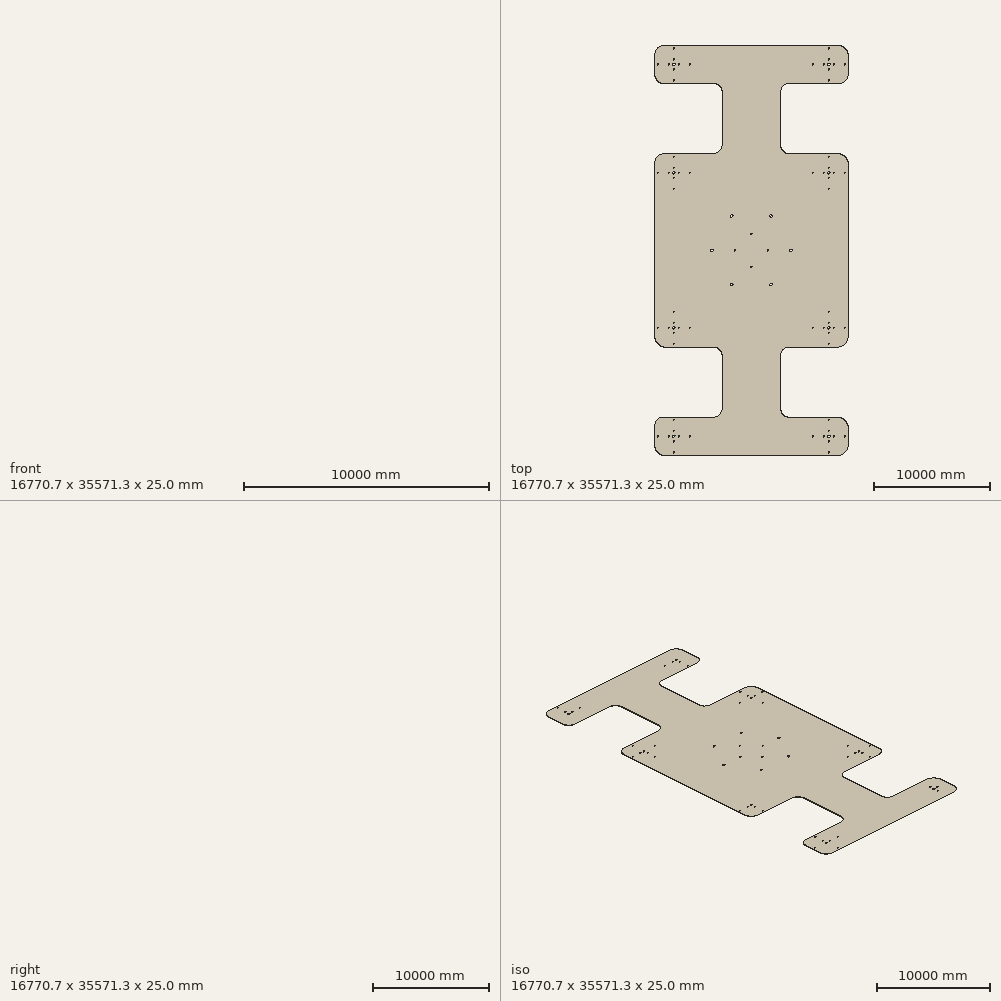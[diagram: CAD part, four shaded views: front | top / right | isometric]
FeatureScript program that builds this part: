
annotation { "Feature Type Name" : "Feature", "Feature Type Description" : "" }
export const myFeature = defineFeature(function(context is Context, id is Id, definition is map)
    precondition{}
    {
        {
            var Q0;
            Q0=qCreatedBy(makeId("Top.planeOp"),FACE);
            var sketch = newSketch(context, id + "F0", { "sketchPlane" : qUnion([Q0])});
            skLineSegment(sketch, "E0", {"start": v(-53625.62, -35381.23) * mm, "end": v(18764.38, -35381.23) * mm});
            skLineSegment(sketch, "E1", {"start": v(-52609.62, -34873.23) * mm, "end": v(17748.38, -34873.23) * mm});
            skLineSegment(sketch, "E2", {"start": v(-52609.62, -34767.82) * mm, "end": v(17748.38, -34767.82) * mm});
            skLineSegment(sketch, "E3", {"start": v(-52609.62, -34978.64) * mm, "end": v(17748.38, -34978.64) * mm});
            skLineSegment(sketch, "E4", {"start": v(-52609.62, -34365.23) * mm, "end": v(17748.38, -34365.23) * mm});
            skLineSegment(sketch, "E5", {"start": v(18764.38, -35381.23) * mm, "end": v(18764.38, -28777.23) * mm});
            skLineSegment(sketch, "E6", {"start": v(18256.38, -35381.23) * mm, "end": v(18256.38, -28777.23) * mm});
            skLineSegment(sketch, "E7", {"start": v(18150.97, -35381.23) * mm, "end": v(18150.97, -28777.23) * mm});
            skLineSegment(sketch, "E8", {"start": v(18361.79, -35381.23) * mm, "end": v(18361.79, -28777.23) * mm});
            skLineSegment(sketch, "E9", {"start": v(17748.38, -35381.23) * mm, "end": v(17748.38, -28777.23) * mm});
            skLineSegment(sketch, "E10", {"start": v(-53625.62, -35381.23) * mm, "end": v(-53625.62, -28777.23) * mm});
            skLineSegment(sketch, "E11", {"start": v(-53117.62, -35381.23) * mm, "end": v(-53117.62, -28777.23) * mm});
            skLineSegment(sketch, "E12", {"start": v(-53012.21, -35381.23) * mm, "end": v(-53012.21, -28777.23) * mm});
            skLineSegment(sketch, "E13", {"start": v(-53223.03, -35381.23) * mm, "end": v(-53223.03, -28777.23) * mm});
            skLineSegment(sketch, "E14", {"start": v(-52609.62, -35381.23) * mm, "end": v(-52609.62, -28777.23) * mm});
            skLineSegment(sketch, "E15", {"start": v(-52609.62, -29793.23) * mm, "end": v(17748.38, -29793.23) * mm});
            skLineSegment(sketch, "E16", {"start": v(-52609.62, -29285.23) * mm, "end": v(17748.38, -29285.23) * mm});
            skLineSegment(sketch, "E17", {"start": v(-52609.62, -29179.82) * mm, "end": v(17748.38, -29179.82) * mm});
            skLineSegment(sketch, "E18", {"start": v(-52609.62, -29390.64) * mm, "end": v(17748.38, -29390.64) * mm});
            skLineSegment(sketch, "E19", {"start": v(-53625.62, -28777.23) * mm, "end": v(18764.38, -28777.23) * mm});
            skLineSegment(sketch, "E20", {"start": v(15843.38, -6425.23) * mm, "end": v(15843.38, -17601.23) * mm});
            skLineSegment(sketch, "E21", {"start": v(15335.38, -6425.23) * mm, "end": v(15335.38, -17601.23) * mm});
            skLineSegment(sketch, "E22", {"start": v(14827.38, -6425.23) * mm, "end": v(14827.38, -17601.23) * mm});
            skLineSegment(sketch, "E23", {"start": v(15229.97, -6425.23) * mm, "end": v(15229.97, -17601.23) * mm});
            skLineSegment(sketch, "E24", {"start": v(15440.79, -6425.23) * mm, "end": v(15440.79, -17601.23) * mm});
            skLineSegment(sketch, "E25", {"start": v(-5492.62, -6425.23) * mm, "end": v(-5492.62, -17601.23) * mm});
            skLineSegment(sketch, "E26", {"start": v(-6000.62, -6425.23) * mm, "end": v(-6000.62, -17601.23) * mm});
            skLineSegment(sketch, "E27", {"start": v(-5895.21, -6425.23) * mm, "end": v(-5895.21, -17601.23) * mm});
            skLineSegment(sketch, "E28", {"start": v(-6106.03, -6425.23) * mm, "end": v(-6106.03, -17601.23) * mm});
            skLineSegment(sketch, "E29", {"start": v(-6508.62, -6425.23) * mm, "end": v(-6508.62, -17601.23) * mm});
            skLineSegment(sketch, "E30", {"start": v(15843.38, -28777.23) * mm, "end": v(15843.38, -17601.23) * mm});
            skLineSegment(sketch, "E31", {"start": v(15335.38, -28777.23) * mm, "end": v(15335.38, -17601.23) * mm});
            skLineSegment(sketch, "E32", {"start": v(15440.79, -28777.23) * mm, "end": v(15440.79, -17601.23) * mm});
            skLineSegment(sketch, "E33", {"start": v(15229.97, -28777.23) * mm, "end": v(15229.97, -17601.23) * mm});
            skLineSegment(sketch, "E34", {"start": v(14827.38, -28777.23) * mm, "end": v(14827.38, -17601.23) * mm});
            skLineSegment(sketch, "E35", {"start": v(-5492.62, -28777.23) * mm, "end": v(-5492.62, -17601.23) * mm});
            skLineSegment(sketch, "E36", {"start": v(-6000.62, -28777.23) * mm, "end": v(-6000.62, -17601.23) * mm});
            skLineSegment(sketch, "E37", {"start": v(-5895.21, -28777.23) * mm, "end": v(-5895.21, -17601.23) * mm});
            skLineSegment(sketch, "E38", {"start": v(-6106.03, -28777.23) * mm, "end": v(-6106.03, -17601.23) * mm});
            skLineSegment(sketch, "E39", {"start": v(-6508.62, -28777.23) * mm, "end": v(-6508.62, -17601.23) * mm});
            skLineSegment(sketch, "E40", {"start": v(-17430.62, -17601.23) * mm, "end": v(15843.38, -17601.23) * mm});
            skLineSegment(sketch, "E41", {"start": v(-10826.62, -29793.23) * mm, "end": v(15843.38, -29793.23) * mm});
            skLineSegment(sketch, "E42", {"start": v(-10826.62, -29285.23) * mm, "end": v(15843.38, -29285.23) * mm});
            skLineSegment(sketch, "E43", {"start": v(-10826.62, -29179.82) * mm, "end": v(15843.38, -29179.82) * mm});
            skLineSegment(sketch, "E44", {"start": v(-10826.62, -29390.64) * mm, "end": v(15843.38, -29390.64) * mm});
            skLineSegment(sketch, "E45", {"start": v(-10826.62, -28777.23) * mm, "end": v(15843.38, -28777.23) * mm});
            skLineSegment(sketch, "E46", {"start": v(-10826.62, -5409.23) * mm, "end": v(15843.38, -5409.23) * mm});
            skLineSegment(sketch, "E47", {"start": v(-10826.62, -5917.23) * mm, "end": v(15843.38, -5917.23) * mm});
            skLineSegment(sketch, "E48", {"start": v(-10826.62, -6022.64) * mm, "end": v(15843.38, -6022.64) * mm});
            skLineSegment(sketch, "E49", {"start": v(-10826.62, -5811.82) * mm, "end": v(15843.38, -5811.82) * mm});
            skLineSegment(sketch, "E50", {"start": v(-10826.62, -6425.23) * mm, "end": v(15843.38, -6425.23) * mm});
            skLineSegment(sketch, "E51", {"start": v(15843.38, -5409.23) * mm, "end": v(15843.38, -6425.23) * mm});
            skLineSegment(sketch, "E52", {"start": v(15843.38, -28777.23) * mm, "end": v(15843.38, -29793.23) * mm});
            skLineSegment(sketch, "E53", {"start": v(-10826.62, -5409.23) * mm, "end": v(-10826.62, -6425.23) * mm});
            skLineSegment(sketch, "E54", {"start": v(-10826.62, -28777.23) * mm, "end": v(-10826.62, -29793.23) * mm});
            skLineSegment(sketch, "E55", {"start": v(-50704.62, -6425.23) * mm, "end": v(-50704.62, -17601.23) * mm});
            skLineSegment(sketch, "E56", {"start": v(-50196.62, -6425.23) * mm, "end": v(-50196.62, -17601.23) * mm});
            skLineSegment(sketch, "E57", {"start": v(-49688.62, -6425.23) * mm, "end": v(-49688.62, -17601.23) * mm});
            skLineSegment(sketch, "E58", {"start": v(-50091.21, -6425.23) * mm, "end": v(-50091.21, -17601.23) * mm});
            skLineSegment(sketch, "E59", {"start": v(-50302.03, -6425.23) * mm, "end": v(-50302.03, -17601.23) * mm});
            skLineSegment(sketch, "E60", {"start": v(-29368.62, -6425.23) * mm, "end": v(-29368.62, -17601.23) * mm});
            skLineSegment(sketch, "E61", {"start": v(-28860.62, -6425.23) * mm, "end": v(-28860.62, -17601.23) * mm});
            skLineSegment(sketch, "E62", {"start": v(-28966.03, -6425.23) * mm, "end": v(-28966.03, -17601.23) * mm});
            skLineSegment(sketch, "E63", {"start": v(-28755.21, -6425.23) * mm, "end": v(-28755.21, -17601.23) * mm});
            skLineSegment(sketch, "E64", {"start": v(-28352.62, -6425.23) * mm, "end": v(-28352.62, -17601.23) * mm});
            skLineSegment(sketch, "E65", {"start": v(-50704.62, -28777.23) * mm, "end": v(-50704.62, -17601.23) * mm});
            skLineSegment(sketch, "E66", {"start": v(-50196.62, -28777.23) * mm, "end": v(-50196.62, -17601.23) * mm});
            skLineSegment(sketch, "E67", {"start": v(-50302.03, -28777.23) * mm, "end": v(-50302.03, -17601.23) * mm});
            skLineSegment(sketch, "E68", {"start": v(-50091.21, -28777.23) * mm, "end": v(-50091.21, -17601.23) * mm});
            skLineSegment(sketch, "E69", {"start": v(-49688.62, -28777.23) * mm, "end": v(-49688.62, -17601.23) * mm});
            skLineSegment(sketch, "E70", {"start": v(-29368.62, -28777.23) * mm, "end": v(-29368.62, -17601.23) * mm});
            skLineSegment(sketch, "E71", {"start": v(-28860.62, -28777.23) * mm, "end": v(-28860.62, -17601.23) * mm});
            skLineSegment(sketch, "E72", {"start": v(-28966.03, -28777.23) * mm, "end": v(-28966.03, -17601.23) * mm});
            skLineSegment(sketch, "E73", {"start": v(-28755.21, -28777.23) * mm, "end": v(-28755.21, -17601.23) * mm});
            skLineSegment(sketch, "E74", {"start": v(-28352.62, -28777.23) * mm, "end": v(-28352.62, -17601.23) * mm});
            skLineSegment(sketch, "E75", {"start": v(-17430.62, -17601.23) * mm, "end": v(-50704.62, -17601.23) * mm});
            skLineSegment(sketch, "E76", {"start": v(-24034.62, -29793.23) * mm, "end": v(-50704.62, -29793.23) * mm});
            skLineSegment(sketch, "E77", {"start": v(-24034.62, -29285.23) * mm, "end": v(-50704.62, -29285.23) * mm});
            skLineSegment(sketch, "E78", {"start": v(-24034.62, -29179.82) * mm, "end": v(-50704.62, -29179.82) * mm});
            skLineSegment(sketch, "E79", {"start": v(-24034.62, -29390.64) * mm, "end": v(-50704.62, -29390.64) * mm});
            skLineSegment(sketch, "E80", {"start": v(-24034.62, -28777.23) * mm, "end": v(-50704.62, -28777.23) * mm});
            skLineSegment(sketch, "E81", {"start": v(-24034.62, -5409.23) * mm, "end": v(-50704.62, -5409.23) * mm});
            skLineSegment(sketch, "E82", {"start": v(-24034.62, -5917.23) * mm, "end": v(-50704.62, -5917.23) * mm});
            skLineSegment(sketch, "E83", {"start": v(-24034.62, -6022.64) * mm, "end": v(-50704.62, -6022.64) * mm});
            skLineSegment(sketch, "E84", {"start": v(-24034.62, -5811.82) * mm, "end": v(-50704.62, -5811.82) * mm});
            skLineSegment(sketch, "E85", {"start": v(-24034.62, -6425.23) * mm, "end": v(-50704.62, -6425.23) * mm});
            skLineSegment(sketch, "E86", {"start": v(-50704.62, -5409.23) * mm, "end": v(-50704.62, -6425.23) * mm});
            skLineSegment(sketch, "E87", {"start": v(-50704.62, -28777.23) * mm, "end": v(-50704.62, -29793.23) * mm});
            skLineSegment(sketch, "E88", {"start": v(-24034.62, -5409.23) * mm, "end": v(-24034.62, -6425.23) * mm});
            skLineSegment(sketch, "E89", {"start": v(-24034.62, -28777.23) * mm, "end": v(-24034.62, -29793.23) * mm});
            skLineSegment(sketch, "E90", {"start": v(-17430.62, 7443.17) * mm, "end": v(-17430.62, -41629.63) * mm});
            skLineSegment(sketch, "E91", {"start": v(-14382.62, -7441.23) * mm, "end": v(-14382.62, -8457.23) * mm});
            skLineSegment(sketch, "E92", {"start": v(-28352.62, -27761.23) * mm, "end": v(-6508.62, -27761.23) * mm});
            skLineSegment(sketch, "E93", {"start": v(-28352.62, -28269.23) * mm, "end": v(-6508.62, -28269.23) * mm});
            skLineSegment(sketch, "E94", {"start": v(-28352.62, -28163.82) * mm, "end": v(-6508.62, -28163.82) * mm});
            skLineSegment(sketch, "E95", {"start": v(-28352.62, -28374.64) * mm, "end": v(-6508.62, -28374.64) * mm});
            skLineSegment(sketch, "E96", {"start": v(-28352.62, -28777.23) * mm, "end": v(-6508.62, -28777.23) * mm});
            skLineSegment(sketch, "E97", {"start": v(-5492.62, -27761.23) * mm, "end": v(14827.38, -27761.23) * mm});
            skLineSegment(sketch, "E98", {"start": v(-10191.62, -28269.23) * mm, "end": v(14827.38, -28269.23) * mm});
            skLineSegment(sketch, "E99", {"start": v(-5492.62, -28163.82) * mm, "end": v(14827.38, -28163.82) * mm});
            skLineSegment(sketch, "E100", {"start": v(-5492.62, -28374.64) * mm, "end": v(14827.38, -28374.64) * mm});
            skLineSegment(sketch, "E101", {"start": v(-10191.62, -28777.23) * mm, "end": v(14827.38, -28777.23) * mm});
            skLineSegment(sketch, "E102", {"start": v(-49688.62, -27761.23) * mm, "end": v(-29368.62, -27761.23) * mm});
            skLineSegment(sketch, "E103", {"start": v(-49688.62, -28269.23) * mm, "end": v(-29368.62, -28269.23) * mm});
            skLineSegment(sketch, "E104", {"start": v(-49688.62, -28163.82) * mm, "end": v(-29368.62, -28163.82) * mm});
            skLineSegment(sketch, "E105", {"start": v(-49688.62, -28374.64) * mm, "end": v(-29368.62, -28374.64) * mm});
            skLineSegment(sketch, "E106", {"start": v(-49688.62, -28777.23) * mm, "end": v(-29368.62, -28777.23) * mm});
            skLineSegment(sketch, "E107", {"start": v(-28352.62, -7441.23) * mm, "end": v(-6508.62, -7441.23) * mm});
            skLineSegment(sketch, "E108", {"start": v(-28352.62, -6933.23) * mm, "end": v(-6508.62, -6933.23) * mm});
            skLineSegment(sketch, "E109", {"start": v(-28352.62, -7038.64) * mm, "end": v(-6508.62, -7038.64) * mm});
            skLineSegment(sketch, "E110", {"start": v(-28352.62, -6827.82) * mm, "end": v(-6508.62, -6827.82) * mm});
            skLineSegment(sketch, "E111", {"start": v(-28352.62, -6425.23) * mm, "end": v(-6508.62, -6425.23) * mm});
            skLineSegment(sketch, "E112", {"start": v(-5492.62, -7441.23) * mm, "end": v(14827.38, -7441.23) * mm});
            skLineSegment(sketch, "E113", {"start": v(-10191.62, -6933.23) * mm, "end": v(14827.38, -6933.23) * mm});
            skLineSegment(sketch, "E114", {"start": v(-5492.62, -7038.64) * mm, "end": v(14827.38, -7038.64) * mm});
            skLineSegment(sketch, "E115", {"start": v(-5492.62, -6827.82) * mm, "end": v(14827.38, -6827.82) * mm});
            skLineSegment(sketch, "E116", {"start": v(-49688.62, -7441.23) * mm, "end": v(-29368.62, -7441.23) * mm});
            skLineSegment(sketch, "E117", {"start": v(-49688.62, -6933.23) * mm, "end": v(-29368.62, -6933.23) * mm});
            skLineSegment(sketch, "E118", {"start": v(-49688.62, -7038.64) * mm, "end": v(-29368.62, -7038.64) * mm});
            skLineSegment(sketch, "E119", {"start": v(-49688.62, -6827.82) * mm, "end": v(-29368.62, -6827.82) * mm});
            skLineSegment(sketch, "E120", {"start": v(-14382.62, -8457.23) * mm, "end": v(-6508.62, -8457.23) * mm});
            skLineSegment(sketch, "E121", {"start": v(-14382.62, -7949.23) * mm, "end": v(-6508.62, -7949.23) * mm});
            skLineSegment(sketch, "E122", {"start": v(-14382.62, -8054.64) * mm, "end": v(-6508.62, -8054.64) * mm});
            skLineSegment(sketch, "E123", {"start": v(-14382.62, -7843.82) * mm, "end": v(-6508.62, -7843.82) * mm});
            skCircle(sketch, "E124", {"center": v(51353.06, -10870.23) * mm, "radius": 1397 * mm});
            skLineSegment(sketch, "E125", {"start": v(51353.06, -9219.23) * mm, "end": v(51353.06, -12521.23) * mm});
            skLineSegment(sketch, "E126", {"start": v(49716.24, -10870.23) * mm, "end": v(53018.24, -10870.23) * mm});
            skLineSegment(sketch, "E127", {"start": v(52369.06, -10870.23) * mm, "end": v(50337.06, -10870.23) * mm});
            skLineSegment(sketch, "E128", {"start": v(51353.06, -9854.23) * mm, "end": v(51353.06, -11886.23) * mm});
            skCircle(sketch, "E129", {"center": v(51353.06, -10870.23) * mm, "radius": 444.5 * mm});
            skCircle(sketch, "E130", {"center": v(51371.33, -10392.3) * mm, "radius": 6.35 * mm});
            skLineSegment(sketch, "E131", {"start": v(51353.06, -10324.13) * mm, "end": v(51353.06, -10527.33) * mm});
            skLineSegment(sketch, "E132", {"start": v(51251.46, -10425.73) * mm, "end": v(51454.66, -10425.73) * mm});
            skCircle(sketch, "E133", {"center": v(51353.06, -10425.73) * mm, "radius": 62.45 * mm});
            skArc(sketch, "E134", {"start": v(51276.86, -10425.73) * mm, "mid": v(51299.18, -10479.61) * mm, "end": v(51353.06, -10501.93) * mm});
            skCircle(sketch, "E135", {"center": v(50875.13, -10851.96) * mm, "radius": 6.35 * mm});
            skLineSegment(sketch, "E136", {"start": v(50806.96, -10870.23) * mm, "end": v(51010.16, -10870.23) * mm});
            skLineSegment(sketch, "E137", {"start": v(50908.56, -10971.83) * mm, "end": v(50908.56, -10768.63) * mm});
            skCircle(sketch, "E138", {"center": v(50908.56, -10870.23) * mm, "radius": 62.45 * mm});
            skArc(sketch, "E139", {"start": v(50908.56, -10946.43) * mm, "mid": v(50962.45, -10924.11) * mm, "end": v(50984.76, -10870.23) * mm});
            skCircle(sketch, "E140", {"center": v(51334.8, -11348.17) * mm, "radius": 6.35 * mm});
            skLineSegment(sketch, "E141", {"start": v(51353.06, -11416.33) * mm, "end": v(51353.06, -11213.13) * mm});
            skLineSegment(sketch, "E142", {"start": v(51454.66, -11314.73) * mm, "end": v(51251.46, -11314.73) * mm});
            skCircle(sketch, "E143", {"center": v(51353.06, -11314.73) * mm, "radius": 62.45 * mm});
            skArc(sketch, "E144", {"start": v(51429.26, -11314.73) * mm, "mid": v(51406.95, -11260.85) * mm, "end": v(51353.06, -11238.53) * mm});
            skCircle(sketch, "E145", {"center": v(51831, -10888.5) * mm, "radius": 6.35 * mm});
            skLineSegment(sketch, "E146", {"start": v(51899.16, -10870.23) * mm, "end": v(51695.96, -10870.23) * mm});
            skLineSegment(sketch, "E147", {"start": v(51797.56, -10768.63) * mm, "end": v(51797.56, -10971.83) * mm});
            skCircle(sketch, "E148", {"center": v(51797.56, -10870.23) * mm, "radius": 62.45 * mm});
            skArc(sketch, "E149", {"start": v(51797.56, -10794.03) * mm, "mid": v(51743.68, -10816.35) * mm, "end": v(51721.36, -10870.23) * mm});
            skCircle(sketch, "E150", {"center": v(51380.17, -10885.04) * mm, "radius": 6.35 * mm});
            skCircle(sketch, "E151", {"center": v(51353.06, -10870.23) * mm, "radius": 108.79 * mm});
            skArc(sketch, "E152", {"start": v(51340.22, -10747.43) * mm, "mid": v(51257.14, -10792.48) * mm, "end": v(51230.26, -10883.08) * mm});
            skLineSegment(sketch, "E153", {"start": v(51502, -10870.23) * mm, "end": v(51204.12, -10870.23) * mm});
            skLineSegment(sketch, "E154", {"start": v(51353.06, -10721.28) * mm, "end": v(51353.06, -11019.18) * mm});
            skLineSegment(sketch, "E155", {"start": v(52496.06, -10870.23) * mm, "end": v(50210.06, -10870.23) * mm});
            skLineSegment(sketch, "E156", {"start": v(51353.06, -12394.23) * mm, "end": v(51353.06, -12140.23) * mm});
            skLineSegment(sketch, "E157", {"start": v(51480.06, -12267.23) * mm, "end": v(51226.06, -12267.23) * mm});
            skCircle(sketch, "E158", {"center": v(51353.06, -12267.23) * mm, "radius": 62.45 * mm});
            skArc(sketch, "E159", {"start": v(51429.26, -12267.23) * mm, "mid": v(51406.95, -12213.35) * mm, "end": v(51353.06, -12191.03) * mm});
            skLineSegment(sketch, "E160", {"start": v(49956.06, -10997.23) * mm, "end": v(49956.06, -10743.23) * mm});
            skLineSegment(sketch, "E161", {"start": v(50083.06, -10870.23) * mm, "end": v(49829.06, -10870.23) * mm});
            skCircle(sketch, "E162", {"center": v(49956.06, -10870.23) * mm, "radius": 62.45 * mm});
            skArc(sketch, "E163", {"start": v(50032.26, -10870.23) * mm, "mid": v(50009.95, -10816.35) * mm, "end": v(49956.06, -10794.03) * mm});
            skLineSegment(sketch, "E164", {"start": v(51353.06, -9600.23) * mm, "end": v(51353.06, -9346.23) * mm});
            skLineSegment(sketch, "E165", {"start": v(51480.06, -9473.23) * mm, "end": v(51226.06, -9473.23) * mm});
            skCircle(sketch, "E166", {"center": v(51353.06, -9473.23) * mm, "radius": 62.45 * mm});
            skArc(sketch, "E167", {"start": v(51429.26, -9473.23) * mm, "mid": v(51406.95, -9419.35) * mm, "end": v(51353.06, -9397.03) * mm});
            skLineSegment(sketch, "E168", {"start": v(52750.06, -10997.23) * mm, "end": v(52750.06, -10743.23) * mm});
            skLineSegment(sketch, "E169", {"start": v(52877.06, -10870.23) * mm, "end": v(52623.06, -10870.23) * mm});
            skCircle(sketch, "E170", {"center": v(52750.06, -10870.23) * mm, "radius": 62.45 * mm});
            skArc(sketch, "E171", {"start": v(52826.26, -10870.23) * mm, "mid": v(52803.95, -10816.35) * mm, "end": v(52750.06, -10794.03) * mm});
            skLineSegment(sketch, "E172", {"start": v(44622.06, -26607.16) * mm, "end": v(44622.06, 178.77) * mm});
            skLineSegment(sketch, "E173", {"start": v(35628.8, -17601.23) * mm, "end": v(53625.62, -17601.23) * mm});
            skCircle(sketch, "E174", {"center": v(44622.06, -17601.23) * mm, "radius": 3429 * mm});
            skCircle(sketch, "E175", {"center": v(44622.06, -17601.23) * mm, "radius": 1397 * mm});
            skLineSegment(sketch, "E176", {"start": v(42971.06, -17601.23) * mm, "end": v(46273.06, -17601.23) * mm});
            skLineSegment(sketch, "E177", {"start": v(44622.06, -15950.23) * mm, "end": v(44622.06, -19252.23) * mm});
            skLineSegment(sketch, "E178", {"start": v(44622.06, -18617.23) * mm, "end": v(44622.06, -16585.23) * mm});
            skLineSegment(sketch, "E179", {"start": v(43606.06, -17601.23) * mm, "end": v(45638.06, -17601.23) * mm});
            skLineSegment(sketch, "E180", {"start": v(44622.06, -18744.23) * mm, "end": v(44622.06, -16458.23) * mm});
            skLineSegment(sketch, "E181", {"start": v(43098.06, -17601.23) * mm, "end": v(43352.06, -17601.23) * mm});
            skLineSegment(sketch, "E182", {"start": v(43225.06, -17474.23) * mm, "end": v(43225.06, -17728.23) * mm});
            skCircle(sketch, "E183", {"center": v(43225.06, -17601.23) * mm, "radius": 62.45 * mm});
            skArc(sketch, "E184", {"start": v(43301.26, -17601.23) * mm, "mid": v(43278.95, -17547.35) * mm, "end": v(43225.06, -17525.03) * mm});
            skLineSegment(sketch, "E185", {"start": v(44495.06, -18998.23) * mm, "end": v(44749.06, -18998.23) * mm});
            skLineSegment(sketch, "E186", {"start": v(44622.06, -18871.23) * mm, "end": v(44622.06, -19125.23) * mm});
            skCircle(sketch, "E187", {"center": v(44622.06, -18998.23) * mm, "radius": 62.45 * mm});
            skArc(sketch, "E188", {"start": v(44698.26, -18998.23) * mm, "mid": v(44675.95, -18944.35) * mm, "end": v(44622.06, -18922.03) * mm});
            skLineSegment(sketch, "E189", {"start": v(45892.06, -17601.23) * mm, "end": v(46146.06, -17601.23) * mm});
            skLineSegment(sketch, "E190", {"start": v(46019.06, -17474.23) * mm, "end": v(46019.06, -17728.23) * mm});
            skCircle(sketch, "E191", {"center": v(46019.06, -17601.23) * mm, "radius": 62.45 * mm});
            skArc(sketch, "E192", {"start": v(46095.26, -17601.23) * mm, "mid": v(46072.95, -17547.35) * mm, "end": v(46019.06, -17525.03) * mm});
            skLineSegment(sketch, "E193", {"start": v(44495.06, -16204.23) * mm, "end": v(44749.06, -16204.23) * mm});
            skLineSegment(sketch, "E194", {"start": v(44622.06, -16077.23) * mm, "end": v(44622.06, -16331.23) * mm});
            skCircle(sketch, "E195", {"center": v(44622.06, -16204.23) * mm, "radius": 62.45 * mm});
            skArc(sketch, "E196", {"start": v(44698.26, -16204.23) * mm, "mid": v(44675.95, -16150.35) * mm, "end": v(44622.06, -16128.03) * mm});
            skCircle(sketch, "E197", {"center": v(48051.06, -17601.23) * mm, "radius": 114.3 * mm});
            skCircle(sketch, "E198", {"center": v(48051.06, -17601.23) * mm, "radius": 177.8 * mm});
            skLineSegment(sketch, "E199", {"start": v(48051.06, -17839.99) * mm, "end": v(48051.06, -17362.47) * mm});
            skLineSegment(sketch, "E200", {"start": v(47812.3, -17601.23) * mm, "end": v(48289.82, -17601.23) * mm});
            skCircle(sketch, "E201", {"center": v(46336.56, -20570.83) * mm, "radius": 114.3 * mm});
            skCircle(sketch, "E202", {"center": v(46336.56, -20570.83) * mm, "radius": 177.8 * mm});
            skLineSegment(sketch, "E203", {"start": v(46129.8, -20690.21) * mm, "end": v(46543.34, -20451.45) * mm});
            skLineSegment(sketch, "E204", {"start": v(46217.18, -20364.06) * mm, "end": v(46455.94, -20777.6) * mm});
            skCircle(sketch, "E205", {"center": v(42907.56, -20570.83) * mm, "radius": 114.3 * mm});
            skCircle(sketch, "E206", {"center": v(42907.56, -20570.83) * mm, "radius": 177.8 * mm});
            skLineSegment(sketch, "E207", {"start": v(42700.8, -20451.45) * mm, "end": v(43114.34, -20690.21) * mm});
            skLineSegment(sketch, "E208", {"start": v(43026.94, -20364.06) * mm, "end": v(42788.18, -20777.6) * mm});
            skCircle(sketch, "E209", {"center": v(41193.06, -17601.23) * mm, "radius": 114.3 * mm});
            skCircle(sketch, "E210", {"center": v(41193.06, -17601.23) * mm, "radius": 177.8 * mm});
            skLineSegment(sketch, "E211", {"start": v(41193.06, -17362.47) * mm, "end": v(41193.06, -17839.99) * mm});
            skLineSegment(sketch, "E212", {"start": v(41431.82, -17601.23) * mm, "end": v(40954.3, -17601.23) * mm});
            skCircle(sketch, "E213", {"center": v(42907.56, -14631.63) * mm, "radius": 114.3 * mm});
            skCircle(sketch, "E214", {"center": v(42907.56, -14631.63) * mm, "radius": 177.8 * mm});
            skLineSegment(sketch, "E215", {"start": v(43114.34, -14512.25) * mm, "end": v(42700.8, -14751) * mm});
            skLineSegment(sketch, "E216", {"start": v(43026.94, -14838.4) * mm, "end": v(42788.18, -14424.86) * mm});
            skCircle(sketch, "E217", {"center": v(46336.56, -14631.63) * mm, "radius": 114.3 * mm});
            skCircle(sketch, "E218", {"center": v(46336.56, -14631.63) * mm, "radius": 177.8 * mm});
            skLineSegment(sketch, "E219", {"start": v(46543.34, -14751) * mm, "end": v(46129.8, -14512.25) * mm});
            skLineSegment(sketch, "E220", {"start": v(46217.18, -14838.4) * mm, "end": v(46455.94, -14424.86) * mm});
            skLineSegment(sketch, "E221", {"start": v(47162.06, -3885.23) * mm, "end": v(47162.06, -8457.23) * mm});
            skArc(sketch, "E222", {"start": v(47162.06, -8457.23) * mm, "mid": v(48462.88, -7918.41) * mm, "end": v(47924.06, -9219.23) * mm});
            skLineSegment(sketch, "E223", {"start": v(47924.06, -9219.23) * mm, "end": v(52242.06, -9219.23) * mm});
            skLineSegment(sketch, "E224", {"start": v(52242.06, -9219.23) * mm, "end": v(53004.06, -9981.23) * mm});
            skLineSegment(sketch, "E225", {"start": v(53004.06, -9981.23) * mm, "end": v(53004.06, -25221.23) * mm});
            skLineSegment(sketch, "E226", {"start": v(53004.06, -25221.23) * mm, "end": v(52242.06, -25983.23) * mm});
            skLineSegment(sketch, "E227", {"start": v(52242.06, -25983.23) * mm, "end": v(47924.06, -25983.23) * mm});
            skArc(sketch, "E228", {"start": v(47924.06, -25983.23) * mm, "mid": v(48462.88, -27284.05) * mm, "end": v(47162.06, -26745.23) * mm});
            skLineSegment(sketch, "E229", {"start": v(47162.06, -26745.23) * mm, "end": v(47162.06, -31317.23) * mm});
            skArc(sketch, "E230", {"start": v(47162.06, -31317.23) * mm, "mid": v(48462.88, -30778.41) * mm, "end": v(47924.06, -32079.23) * mm});
            skLineSegment(sketch, "E231", {"start": v(47924.06, -32079.23) * mm, "end": v(52242.06, -32079.23) * mm});
            skCircle(sketch, "E232", {"center": v(51353.06, -24332.23) * mm, "radius": 1397 * mm});
            skLineSegment(sketch, "E233", {"start": v(53004.06, -24332.23) * mm, "end": v(49702.06, -24332.23) * mm});
            skLineSegment(sketch, "E234", {"start": v(51353.06, -22695.4) * mm, "end": v(51353.06, -25997.4) * mm});
            skLineSegment(sketch, "E235", {"start": v(51353.06, -25348.23) * mm, "end": v(51353.06, -23316.23) * mm});
            skLineSegment(sketch, "E236", {"start": v(52369.06, -24332.23) * mm, "end": v(50337.06, -24332.23) * mm});
            skCircle(sketch, "E237", {"center": v(51353.06, -24332.23) * mm, "radius": 444.5 * mm});
            skCircle(sketch, "E238", {"center": v(51831, -24350.5) * mm, "radius": 6.35 * mm});
            skLineSegment(sketch, "E239", {"start": v(51899.16, -24332.23) * mm, "end": v(51695.96, -24332.23) * mm});
            skLineSegment(sketch, "E240", {"start": v(51797.56, -24230.63) * mm, "end": v(51797.56, -24433.83) * mm});
            skCircle(sketch, "E241", {"center": v(51797.56, -24332.23) * mm, "radius": 62.45 * mm});
            skArc(sketch, "E242", {"start": v(51797.56, -24256.03) * mm, "mid": v(51743.68, -24278.35) * mm, "end": v(51721.36, -24332.23) * mm});
            skCircle(sketch, "E243", {"center": v(51371.33, -23854.3) * mm, "radius": 6.35 * mm});
            skLineSegment(sketch, "E244", {"start": v(51353.06, -23786.13) * mm, "end": v(51353.06, -23989.33) * mm});
            skLineSegment(sketch, "E245", {"start": v(51251.46, -23887.73) * mm, "end": v(51454.66, -23887.73) * mm});
            skCircle(sketch, "E246", {"center": v(51353.06, -23887.73) * mm, "radius": 62.45 * mm});
            skArc(sketch, "E247", {"start": v(51276.86, -23887.73) * mm, "mid": v(51299.18, -23941.61) * mm, "end": v(51353.06, -23963.93) * mm});
            skCircle(sketch, "E248", {"center": v(50875.13, -24313.96) * mm, "radius": 6.35 * mm});
            skLineSegment(sketch, "E249", {"start": v(50806.96, -24332.23) * mm, "end": v(51010.16, -24332.23) * mm});
            skLineSegment(sketch, "E250", {"start": v(50908.56, -24433.83) * mm, "end": v(50908.56, -24230.63) * mm});
            skCircle(sketch, "E251", {"center": v(50908.56, -24332.23) * mm, "radius": 62.45 * mm});
            skArc(sketch, "E252", {"start": v(50908.56, -24408.43) * mm, "mid": v(50962.45, -24386.11) * mm, "end": v(50984.76, -24332.23) * mm});
            skCircle(sketch, "E253", {"center": v(51334.8, -24810.17) * mm, "radius": 6.35 * mm});
            skLineSegment(sketch, "E254", {"start": v(51353.06, -24878.33) * mm, "end": v(51353.06, -24675.13) * mm});
            skLineSegment(sketch, "E255", {"start": v(51454.66, -24776.73) * mm, "end": v(51251.46, -24776.73) * mm});
            skCircle(sketch, "E256", {"center": v(51353.06, -24776.73) * mm, "radius": 62.45 * mm});
            skArc(sketch, "E257", {"start": v(51429.26, -24776.73) * mm, "mid": v(51406.95, -24722.85) * mm, "end": v(51353.06, -24700.53) * mm});
            skCircle(sketch, "E258", {"center": v(51338.26, -24359.34) * mm, "radius": 6.35 * mm});
            skCircle(sketch, "E259", {"center": v(51353.06, -24332.23) * mm, "radius": 108.79 * mm});
            skArc(sketch, "E260", {"start": v(51475.87, -24319.38) * mm, "mid": v(51430.81, -24236.3) * mm, "end": v(51340.22, -24209.43) * mm});
            skLineSegment(sketch, "E261", {"start": v(51353.06, -24481.18) * mm, "end": v(51353.06, -24183.28) * mm});
            skLineSegment(sketch, "E262", {"start": v(51502, -24332.23) * mm, "end": v(51204.12, -24332.23) * mm});
            skLineSegment(sketch, "E263", {"start": v(51353.06, -25475.23) * mm, "end": v(51353.06, -23189.23) * mm});
            skLineSegment(sketch, "E264", {"start": v(49829.06, -24332.23) * mm, "end": v(50083.06, -24332.23) * mm});
            skLineSegment(sketch, "E265", {"start": v(49956.06, -24459.23) * mm, "end": v(49956.06, -24205.23) * mm});
            skCircle(sketch, "E266", {"center": v(49956.06, -24332.23) * mm, "radius": 62.45 * mm});
            skArc(sketch, "E267", {"start": v(49956.06, -24408.43) * mm, "mid": v(50009.95, -24386.11) * mm, "end": v(50032.26, -24332.23) * mm});
            skLineSegment(sketch, "E268", {"start": v(51226.06, -22935.23) * mm, "end": v(51480.06, -22935.23) * mm});
            skLineSegment(sketch, "E269", {"start": v(51353.06, -23062.23) * mm, "end": v(51353.06, -22808.23) * mm});
            skCircle(sketch, "E270", {"center": v(51353.06, -22935.23) * mm, "radius": 62.45 * mm});
            skArc(sketch, "E271", {"start": v(51353.06, -23011.43) * mm, "mid": v(51406.95, -22989.11) * mm, "end": v(51429.26, -22935.23) * mm});
            skLineSegment(sketch, "E272", {"start": v(52623.06, -24332.23) * mm, "end": v(52877.06, -24332.23) * mm});
            skLineSegment(sketch, "E273", {"start": v(52750.06, -24459.23) * mm, "end": v(52750.06, -24205.23) * mm});
            skCircle(sketch, "E274", {"center": v(52750.06, -24332.23) * mm, "radius": 62.45 * mm});
            skArc(sketch, "E275", {"start": v(52750.06, -24408.43) * mm, "mid": v(52803.95, -24386.11) * mm, "end": v(52826.26, -24332.23) * mm});
            skLineSegment(sketch, "E276", {"start": v(51226.06, -25729.23) * mm, "end": v(51480.06, -25729.23) * mm});
            skLineSegment(sketch, "E277", {"start": v(51353.06, -25856.23) * mm, "end": v(51353.06, -25602.23) * mm});
            skCircle(sketch, "E278", {"center": v(51353.06, -25729.23) * mm, "radius": 62.45 * mm});
            skArc(sketch, "E279", {"start": v(51353.06, -25805.43) * mm, "mid": v(51406.95, -25783.11) * mm, "end": v(51429.26, -25729.23) * mm});
            skCircle(sketch, "E280", {"center": v(37891.06, -24332.23) * mm, "radius": 1397 * mm});
            skLineSegment(sketch, "E281", {"start": v(37891.06, -25983.23) * mm, "end": v(37891.06, -22681.23) * mm});
            skLineSegment(sketch, "E282", {"start": v(39527.89, -24332.23) * mm, "end": v(36225.89, -24332.23) * mm});
            skLineSegment(sketch, "E283", {"start": v(36875.06, -24332.23) * mm, "end": v(38907.06, -24332.23) * mm});
            skLineSegment(sketch, "E284", {"start": v(37891.06, -25348.23) * mm, "end": v(37891.06, -23316.23) * mm});
            skCircle(sketch, "E285", {"center": v(37891.06, -24332.23) * mm, "radius": 444.5 * mm});
            skCircle(sketch, "E286", {"center": v(37872.8, -24810.17) * mm, "radius": 6.35 * mm});
            skLineSegment(sketch, "E287", {"start": v(37891.06, -24878.33) * mm, "end": v(37891.06, -24675.13) * mm});
            skLineSegment(sketch, "E288", {"start": v(37992.66, -24776.73) * mm, "end": v(37789.46, -24776.73) * mm});
            skCircle(sketch, "E289", {"center": v(37891.06, -24776.73) * mm, "radius": 62.45 * mm});
            skArc(sketch, "E290", {"start": v(37967.26, -24776.73) * mm, "mid": v(37944.95, -24722.85) * mm, "end": v(37891.06, -24700.53) * mm});
            skCircle(sketch, "E291", {"center": v(38369, -24350.5) * mm, "radius": 6.35 * mm});
            skLineSegment(sketch, "E292", {"start": v(38437.16, -24332.23) * mm, "end": v(38233.96, -24332.23) * mm});
            skLineSegment(sketch, "E293", {"start": v(38335.56, -24230.63) * mm, "end": v(38335.56, -24433.83) * mm});
            skCircle(sketch, "E294", {"center": v(38335.56, -24332.23) * mm, "radius": 62.45 * mm});
            skArc(sketch, "E295", {"start": v(38335.56, -24256.03) * mm, "mid": v(38281.68, -24278.35) * mm, "end": v(38259.36, -24332.23) * mm});
            skCircle(sketch, "E296", {"center": v(37909.33, -23854.3) * mm, "radius": 6.35 * mm});
            skLineSegment(sketch, "E297", {"start": v(37891.06, -23786.13) * mm, "end": v(37891.06, -23989.33) * mm});
            skLineSegment(sketch, "E298", {"start": v(37789.46, -23887.73) * mm, "end": v(37992.66, -23887.73) * mm});
            skCircle(sketch, "E299", {"center": v(37891.06, -23887.73) * mm, "radius": 62.45 * mm});
            skArc(sketch, "E300", {"start": v(37814.86, -23887.73) * mm, "mid": v(37837.18, -23941.61) * mm, "end": v(37891.06, -23963.93) * mm});
            skCircle(sketch, "E301", {"center": v(37413.13, -24313.96) * mm, "radius": 6.35 * mm});
            skLineSegment(sketch, "E302", {"start": v(37344.96, -24332.23) * mm, "end": v(37548.16, -24332.23) * mm});
            skLineSegment(sketch, "E303", {"start": v(37446.56, -24433.83) * mm, "end": v(37446.56, -24230.63) * mm});
            skCircle(sketch, "E304", {"center": v(37446.56, -24332.23) * mm, "radius": 62.45 * mm});
            skArc(sketch, "E305", {"start": v(37446.56, -24408.43) * mm, "mid": v(37500.45, -24386.11) * mm, "end": v(37522.76, -24332.23) * mm});
            skCircle(sketch, "E306", {"center": v(37863.96, -24317.42) * mm, "radius": 6.35 * mm});
            skCircle(sketch, "E307", {"center": v(37891.06, -24332.23) * mm, "radius": 108.79 * mm});
            skArc(sketch, "E308", {"start": v(37903.91, -24455.03) * mm, "mid": v(37986.99, -24409.98) * mm, "end": v(38013.87, -24319.38) * mm});
            skLineSegment(sketch, "E309", {"start": v(37742.12, -24332.23) * mm, "end": v(38040, -24332.23) * mm});
            skLineSegment(sketch, "E310", {"start": v(37891.06, -24481.18) * mm, "end": v(37891.06, -24183.28) * mm});
            skLineSegment(sketch, "E311", {"start": v(36748.06, -24332.23) * mm, "end": v(39034.06, -24332.23) * mm});
            skLineSegment(sketch, "E312", {"start": v(37891.06, -22808.23) * mm, "end": v(37891.06, -23062.23) * mm});
            skLineSegment(sketch, "E313", {"start": v(37764.06, -22935.23) * mm, "end": v(38018.06, -22935.23) * mm});
            skCircle(sketch, "E314", {"center": v(37891.06, -22935.23) * mm, "radius": 62.45 * mm});
            skArc(sketch, "E315", {"start": v(37814.86, -22935.23) * mm, "mid": v(37837.18, -22989.11) * mm, "end": v(37891.06, -23011.43) * mm});
            skLineSegment(sketch, "E316", {"start": v(39288.06, -24205.23) * mm, "end": v(39288.06, -24459.23) * mm});
            skLineSegment(sketch, "E317", {"start": v(39161.06, -24332.23) * mm, "end": v(39415.06, -24332.23) * mm});
            skCircle(sketch, "E318", {"center": v(39288.06, -24332.23) * mm, "radius": 62.45 * mm});
            skArc(sketch, "E319", {"start": v(39211.86, -24332.23) * mm, "mid": v(39234.18, -24386.11) * mm, "end": v(39288.06, -24408.43) * mm});
            skLineSegment(sketch, "E320", {"start": v(37891.06, -25602.23) * mm, "end": v(37891.06, -25856.23) * mm});
            skLineSegment(sketch, "E321", {"start": v(37764.06, -25729.23) * mm, "end": v(38018.06, -25729.23) * mm});
            skCircle(sketch, "E322", {"center": v(37891.06, -25729.23) * mm, "radius": 62.45 * mm});
            skArc(sketch, "E323", {"start": v(37814.86, -25729.23) * mm, "mid": v(37837.18, -25783.11) * mm, "end": v(37891.06, -25805.43) * mm});
            skLineSegment(sketch, "E324", {"start": v(36494.06, -24205.23) * mm, "end": v(36494.06, -24459.23) * mm});
            skLineSegment(sketch, "E325", {"start": v(36367.06, -24332.23) * mm, "end": v(36621.06, -24332.23) * mm});
            skCircle(sketch, "E326", {"center": v(36494.06, -24332.23) * mm, "radius": 62.45 * mm});
            skArc(sketch, "E327", {"start": v(36417.86, -24332.23) * mm, "mid": v(36440.18, -24386.11) * mm, "end": v(36494.06, -24408.43) * mm});
            skCircle(sketch, "E328", {"center": v(37891.06, -10870.23) * mm, "radius": 1397 * mm});
            skLineSegment(sketch, "E329", {"start": v(36240.06, -10870.23) * mm, "end": v(39542.06, -10870.23) * mm});
            skLineSegment(sketch, "E330", {"start": v(37891.06, -12507.05) * mm, "end": v(37891.06, -9205.05) * mm});
            skLineSegment(sketch, "E331", {"start": v(37891.06, -9854.23) * mm, "end": v(37891.06, -11886.23) * mm});
            skLineSegment(sketch, "E332", {"start": v(36875.06, -10870.23) * mm, "end": v(38907.06, -10870.23) * mm});
            skCircle(sketch, "E333", {"center": v(37891.06, -10870.23) * mm, "radius": 444.5 * mm});
            skCircle(sketch, "E334", {"center": v(37413.13, -10851.96) * mm, "radius": 6.35 * mm});
            skLineSegment(sketch, "E335", {"start": v(37344.96, -10870.23) * mm, "end": v(37548.16, -10870.23) * mm});
            skLineSegment(sketch, "E336", {"start": v(37446.56, -10971.83) * mm, "end": v(37446.56, -10768.63) * mm});
            skCircle(sketch, "E337", {"center": v(37446.56, -10870.23) * mm, "radius": 62.45 * mm});
            skArc(sketch, "E338", {"start": v(37446.56, -10946.43) * mm, "mid": v(37500.45, -10924.11) * mm, "end": v(37522.76, -10870.23) * mm});
            skCircle(sketch, "E339", {"center": v(37872.8, -11348.17) * mm, "radius": 6.35 * mm});
            skLineSegment(sketch, "E340", {"start": v(37891.06, -11416.33) * mm, "end": v(37891.06, -11213.13) * mm});
            skLineSegment(sketch, "E341", {"start": v(37992.66, -11314.73) * mm, "end": v(37789.46, -11314.73) * mm});
            skCircle(sketch, "E342", {"center": v(37891.06, -11314.73) * mm, "radius": 62.45 * mm});
            skArc(sketch, "E343", {"start": v(37967.26, -11314.73) * mm, "mid": v(37944.95, -11260.85) * mm, "end": v(37891.06, -11238.53) * mm});
            skCircle(sketch, "E344", {"center": v(38369, -10888.5) * mm, "radius": 6.35 * mm});
            skLineSegment(sketch, "E345", {"start": v(38437.16, -10870.23) * mm, "end": v(38233.96, -10870.23) * mm});
            skLineSegment(sketch, "E346", {"start": v(38335.56, -10768.63) * mm, "end": v(38335.56, -10971.83) * mm});
            skCircle(sketch, "E347", {"center": v(38335.56, -10870.23) * mm, "radius": 62.45 * mm});
            skArc(sketch, "E348", {"start": v(38335.56, -10794.03) * mm, "mid": v(38281.68, -10816.35) * mm, "end": v(38259.36, -10870.23) * mm});
            skCircle(sketch, "E349", {"center": v(37909.33, -10392.3) * mm, "radius": 6.35 * mm});
            skLineSegment(sketch, "E350", {"start": v(37891.06, -10324.13) * mm, "end": v(37891.06, -10527.33) * mm});
            skLineSegment(sketch, "E351", {"start": v(37789.46, -10425.73) * mm, "end": v(37992.66, -10425.73) * mm});
            skCircle(sketch, "E352", {"center": v(37891.06, -10425.73) * mm, "radius": 62.45 * mm});
            skArc(sketch, "E353", {"start": v(37814.86, -10425.73) * mm, "mid": v(37837.18, -10479.61) * mm, "end": v(37891.06, -10501.93) * mm});
            skCircle(sketch, "E354", {"center": v(37905.87, -10843.12) * mm, "radius": 6.35 * mm});
            skCircle(sketch, "E355", {"center": v(37891.06, -10870.23) * mm, "radius": 108.79 * mm});
            skArc(sketch, "E356", {"start": v(37768.26, -10883.08) * mm, "mid": v(37813.31, -10966.15) * mm, "end": v(37903.91, -10993.03) * mm});
            skLineSegment(sketch, "E357", {"start": v(37891.06, -10721.28) * mm, "end": v(37891.06, -11019.18) * mm});
            skLineSegment(sketch, "E358", {"start": v(37742.12, -10870.23) * mm, "end": v(38040, -10870.23) * mm});
            skLineSegment(sketch, "E359", {"start": v(37891.06, -9727.23) * mm, "end": v(37891.06, -12013.23) * mm});
            skLineSegment(sketch, "E360", {"start": v(39415.06, -10870.23) * mm, "end": v(39161.06, -10870.23) * mm});
            skLineSegment(sketch, "E361", {"start": v(39288.06, -10743.23) * mm, "end": v(39288.06, -10997.23) * mm});
            skCircle(sketch, "E362", {"center": v(39288.06, -10870.23) * mm, "radius": 62.45 * mm});
            skArc(sketch, "E363", {"start": v(39288.06, -10794.03) * mm, "mid": v(39234.18, -10816.35) * mm, "end": v(39211.86, -10870.23) * mm});
            skLineSegment(sketch, "E364", {"start": v(38018.06, -12267.23) * mm, "end": v(37764.06, -12267.23) * mm});
            skLineSegment(sketch, "E365", {"start": v(37891.06, -12140.23) * mm, "end": v(37891.06, -12394.23) * mm});
            skCircle(sketch, "E366", {"center": v(37891.06, -12267.23) * mm, "radius": 62.45 * mm});
            skArc(sketch, "E367", {"start": v(37891.06, -12191.03) * mm, "mid": v(37837.18, -12213.35) * mm, "end": v(37814.86, -12267.23) * mm});
            skLineSegment(sketch, "E368", {"start": v(36621.06, -10870.23) * mm, "end": v(36367.06, -10870.23) * mm});
            skLineSegment(sketch, "E369", {"start": v(36494.06, -10743.23) * mm, "end": v(36494.06, -10997.23) * mm});
            skCircle(sketch, "E370", {"center": v(36494.06, -10870.23) * mm, "radius": 62.45 * mm});
            skArc(sketch, "E371", {"start": v(36494.06, -10794.03) * mm, "mid": v(36440.18, -10816.35) * mm, "end": v(36417.86, -10870.23) * mm});
            skLineSegment(sketch, "E372", {"start": v(38018.06, -9473.23) * mm, "end": v(37764.06, -9473.23) * mm});
            skLineSegment(sketch, "E373", {"start": v(37891.06, -9346.23) * mm, "end": v(37891.06, -9600.23) * mm});
            skCircle(sketch, "E374", {"center": v(37891.06, -9473.23) * mm, "radius": 62.45 * mm});
            skArc(sketch, "E375", {"start": v(37891.06, -9397.03) * mm, "mid": v(37837.18, -9419.35) * mm, "end": v(37814.86, -9473.23) * mm});
            skLineSegment(sketch, "E376", {"start": v(37891.06, -32093.4) * mm, "end": v(37891.06, -35395.4) * mm});
            skLineSegment(sketch, "E377", {"start": v(37891.06, -34746.23) * mm, "end": v(37891.06, -32714.23) * mm});
            skLineSegment(sketch, "E378", {"start": v(36875.06, -33730.23) * mm, "end": v(38907.06, -33730.23) * mm});
            skCircle(sketch, "E379", {"center": v(37891.06, -33730.23) * mm, "radius": 444.5 * mm});
            skCircle(sketch, "E380", {"center": v(37413.13, -33748.5) * mm, "radius": 6.35 * mm});
            skLineSegment(sketch, "E381", {"start": v(37344.96, -33730.23) * mm, "end": v(37548.16, -33730.23) * mm});
            skLineSegment(sketch, "E382", {"start": v(37446.56, -33628.63) * mm, "end": v(37446.56, -33831.83) * mm});
            skCircle(sketch, "E383", {"center": v(37446.56, -33730.23) * mm, "radius": 62.45 * mm});
            skArc(sketch, "E384", {"start": v(37522.76, -33730.23) * mm, "mid": v(37500.45, -33676.35) * mm, "end": v(37446.56, -33654.03) * mm});
            skCircle(sketch, "E385", {"center": v(37872.8, -33252.3) * mm, "radius": 6.35 * mm});
            skLineSegment(sketch, "E386", {"start": v(37891.06, -33184.13) * mm, "end": v(37891.06, -33387.33) * mm});
            skLineSegment(sketch, "E387", {"start": v(37992.66, -33285.73) * mm, "end": v(37789.46, -33285.73) * mm});
            skCircle(sketch, "E388", {"center": v(37891.06, -33285.73) * mm, "radius": 62.45 * mm});
            skArc(sketch, "E389", {"start": v(37891.06, -33361.93) * mm, "mid": v(37944.95, -33339.61) * mm, "end": v(37967.26, -33285.73) * mm});
            skCircle(sketch, "E390", {"center": v(38369, -33711.96) * mm, "radius": 6.35 * mm});
            skLineSegment(sketch, "E391", {"start": v(38437.16, -33730.23) * mm, "end": v(38233.96, -33730.23) * mm});
            skLineSegment(sketch, "E392", {"start": v(38335.56, -33831.83) * mm, "end": v(38335.56, -33628.63) * mm});
            skCircle(sketch, "E393", {"center": v(38335.56, -33730.23) * mm, "radius": 62.45 * mm});
            skArc(sketch, "E394", {"start": v(38259.36, -33730.23) * mm, "mid": v(38281.68, -33784.11) * mm, "end": v(38335.56, -33806.43) * mm});
            skCircle(sketch, "E395", {"center": v(37909.33, -34208.17) * mm, "radius": 6.35 * mm});
            skLineSegment(sketch, "E396", {"start": v(37891.06, -34276.33) * mm, "end": v(37891.06, -34073.13) * mm});
            skLineSegment(sketch, "E397", {"start": v(37789.46, -34174.73) * mm, "end": v(37992.66, -34174.73) * mm});
            skCircle(sketch, "E398", {"center": v(37891.06, -34174.73) * mm, "radius": 62.45 * mm});
            skArc(sketch, "E399", {"start": v(37891.06, -34098.53) * mm, "mid": v(37837.18, -34120.85) * mm, "end": v(37814.86, -34174.73) * mm});
            skCircle(sketch, "E400", {"center": v(37905.87, -33757.34) * mm, "radius": 6.35 * mm});
            skCircle(sketch, "E401", {"center": v(37891.06, -33730.23) * mm, "radius": 108.79 * mm});
            skArc(sketch, "E402", {"start": v(37903.91, -33607.43) * mm, "mid": v(37813.31, -33634.3) * mm, "end": v(37768.26, -33717.38) * mm});
            skLineSegment(sketch, "E403", {"start": v(37891.06, -33879.18) * mm, "end": v(37891.06, -33581.28) * mm});
            skLineSegment(sketch, "E404", {"start": v(37742.12, -33730.23) * mm, "end": v(38040, -33730.23) * mm});
            skLineSegment(sketch, "E405", {"start": v(37891.06, -34873.23) * mm, "end": v(37891.06, -32587.23) * mm});
            skLineSegment(sketch, "E406", {"start": v(39415.06, -33730.23) * mm, "end": v(39161.06, -33730.23) * mm});
            skLineSegment(sketch, "E407", {"start": v(39288.06, -33857.23) * mm, "end": v(39288.06, -33603.23) * mm});
            skCircle(sketch, "E408", {"center": v(39288.06, -33730.23) * mm, "radius": 62.45 * mm});
            skArc(sketch, "E409", {"start": v(39211.86, -33730.23) * mm, "mid": v(39234.18, -33784.11) * mm, "end": v(39288.06, -33806.43) * mm});
            skLineSegment(sketch, "E410", {"start": v(38018.06, -32333.23) * mm, "end": v(37764.06, -32333.23) * mm});
            skLineSegment(sketch, "E411", {"start": v(37891.06, -32460.23) * mm, "end": v(37891.06, -32206.23) * mm});
            skCircle(sketch, "E412", {"center": v(37891.06, -32333.23) * mm, "radius": 62.45 * mm});
            skArc(sketch, "E413", {"start": v(37814.86, -32333.23) * mm, "mid": v(37837.18, -32387.11) * mm, "end": v(37891.06, -32409.43) * mm});
            skLineSegment(sketch, "E414", {"start": v(36621.06, -33730.23) * mm, "end": v(36367.06, -33730.23) * mm});
            skLineSegment(sketch, "E415", {"start": v(36494.06, -33857.23) * mm, "end": v(36494.06, -33603.23) * mm});
            skCircle(sketch, "E416", {"center": v(36494.06, -33730.23) * mm, "radius": 62.45 * mm});
            skArc(sketch, "E417", {"start": v(36417.86, -33730.23) * mm, "mid": v(36440.18, -33784.11) * mm, "end": v(36494.06, -33806.43) * mm});
            skLineSegment(sketch, "E418", {"start": v(38018.06, -35127.23) * mm, "end": v(37764.06, -35127.23) * mm});
            skLineSegment(sketch, "E419", {"start": v(37891.06, -35254.23) * mm, "end": v(37891.06, -35000.23) * mm});
            skCircle(sketch, "E420", {"center": v(37891.06, -35127.23) * mm, "radius": 62.45 * mm});
            skArc(sketch, "E421", {"start": v(37814.86, -35127.23) * mm, "mid": v(37837.18, -35181.11) * mm, "end": v(37891.06, -35203.43) * mm});
            skLineSegment(sketch, "E422", {"start": v(37002.06, -35381.23) * mm, "end": v(52242.06, -35381.23) * mm});
            skLineSegment(sketch, "E423", {"start": v(53004.06, -34619.23) * mm, "end": v(52242.06, -35381.23) * mm});
            skLineSegment(sketch, "E424", {"start": v(53004.06, -32841.23) * mm, "end": v(52242.06, -32079.23) * mm});
            skLineSegment(sketch, "E425", {"start": v(53004.06, -32841.23) * mm, "end": v(53004.06, -34619.23) * mm});
            skLineSegment(sketch, "E426", {"start": v(36240.06, -32841.23) * mm, "end": v(36240.06, -34619.23) * mm});
            skLineSegment(sketch, "E427", {"start": v(37002.06, -35381.23) * mm, "end": v(36240.06, -34619.23) * mm});
            skLineSegment(sketch, "E428", {"start": v(37002.06, -32079.23) * mm, "end": v(36240.06, -32841.23) * mm});
            skLineSegment(sketch, "E429", {"start": v(37002.06, -32079.23) * mm, "end": v(41320.06, -32079.23) * mm});
            skArc(sketch, "E430", {"start": v(41320.06, -32079.23) * mm, "mid": v(40781.25, -30778.41) * mm, "end": v(42082.06, -31317.23) * mm});
            skLineSegment(sketch, "E431", {"start": v(42082.06, -31317.23) * mm, "end": v(42082.06, -26745.23) * mm});
            skArc(sketch, "E432", {"start": v(42082.06, -26745.23) * mm, "mid": v(40781.25, -27284.05) * mm, "end": v(41320.06, -25983.23) * mm});
            skLineSegment(sketch, "E433", {"start": v(41320.06, -25983.23) * mm, "end": v(37002.06, -25983.23) * mm});
            skLineSegment(sketch, "E434", {"start": v(37002.06, -25983.23) * mm, "end": v(36240.06, -25221.23) * mm});
            skLineSegment(sketch, "E435", {"start": v(36240.06, -25221.23) * mm, "end": v(36240.06, -9981.23) * mm});
            skLineSegment(sketch, "E436", {"start": v(36240.06, -9981.23) * mm, "end": v(37002.06, -9219.23) * mm});
            skLineSegment(sketch, "E437", {"start": v(37002.06, -9219.23) * mm, "end": v(41320.06, -9219.23) * mm});
            skArc(sketch, "E438", {"start": v(41320.06, -9219.23) * mm, "mid": v(40781.25, -7918.41) * mm, "end": v(42082.06, -8457.23) * mm});
            skLineSegment(sketch, "E439", {"start": v(42082.06, -8457.23) * mm, "end": v(42082.06, -3885.23) * mm});
            skArc(sketch, "E440", {"start": v(47162.06, -3885.23) * mm, "mid": v(48462.88, -4424.05) * mm, "end": v(47924.06, -3123.23) * mm});
            skArc(sketch, "E441", {"start": v(41320.06, -3123.23) * mm, "mid": v(40781.25, -4424.05) * mm, "end": v(42082.06, -3885.23) * mm});
            skCircle(sketch, "E442", {"center": v(51353.06, -1472.23) * mm, "radius": 1397 * mm});
            skLineSegment(sketch, "E443", {"start": v(51353.06, 178.77) * mm, "end": v(51353.06, -3123.23) * mm});
            skLineSegment(sketch, "E444", {"start": v(49716.24, -1472.23) * mm, "end": v(53018.24, -1472.23) * mm});
            skLineSegment(sketch, "E445", {"start": v(52369.06, -1472.23) * mm, "end": v(50337.06, -1472.23) * mm});
            skLineSegment(sketch, "E446", {"start": v(51353.06, -456.23) * mm, "end": v(51353.06, -2488.23) * mm});
            skCircle(sketch, "E447", {"center": v(51353.06, -1472.23) * mm, "radius": 444.5 * mm});
            skCircle(sketch, "E448", {"center": v(51371.33, -994.3) * mm, "radius": 6.35 * mm});
            skLineSegment(sketch, "E449", {"start": v(51353.06, -926.13) * mm, "end": v(51353.06, -1129.33) * mm});
            skLineSegment(sketch, "E450", {"start": v(51251.46, -1027.73) * mm, "end": v(51454.66, -1027.73) * mm});
            skCircle(sketch, "E451", {"center": v(51353.06, -1027.73) * mm, "radius": 62.45 * mm});
            skArc(sketch, "E452", {"start": v(51276.86, -1027.73) * mm, "mid": v(51299.18, -1081.61) * mm, "end": v(51353.06, -1103.93) * mm});
            skCircle(sketch, "E453", {"center": v(50875.13, -1453.96) * mm, "radius": 6.35 * mm});
            skLineSegment(sketch, "E454", {"start": v(50806.96, -1472.23) * mm, "end": v(51010.16, -1472.23) * mm});
            skLineSegment(sketch, "E455", {"start": v(50908.56, -1573.83) * mm, "end": v(50908.56, -1370.63) * mm});
            skCircle(sketch, "E456", {"center": v(50908.56, -1472.23) * mm, "radius": 62.45 * mm});
            skArc(sketch, "E457", {"start": v(50908.56, -1548.43) * mm, "mid": v(50962.45, -1526.11) * mm, "end": v(50984.76, -1472.23) * mm});
            skCircle(sketch, "E458", {"center": v(51334.8, -1950.17) * mm, "radius": 6.35 * mm});
            skLineSegment(sketch, "E459", {"start": v(51353.06, -2018.33) * mm, "end": v(51353.06, -1815.13) * mm});
            skLineSegment(sketch, "E460", {"start": v(51454.66, -1916.73) * mm, "end": v(51251.46, -1916.73) * mm});
            skCircle(sketch, "E461", {"center": v(51353.06, -1916.73) * mm, "radius": 62.45 * mm});
            skArc(sketch, "E462", {"start": v(51429.26, -1916.73) * mm, "mid": v(51406.95, -1862.85) * mm, "end": v(51353.06, -1840.53) * mm});
            skCircle(sketch, "E463", {"center": v(51831, -1490.5) * mm, "radius": 6.35 * mm});
            skLineSegment(sketch, "E464", {"start": v(51899.16, -1472.23) * mm, "end": v(51695.96, -1472.23) * mm});
            skLineSegment(sketch, "E465", {"start": v(51797.56, -1370.63) * mm, "end": v(51797.56, -1573.83) * mm});
            skCircle(sketch, "E466", {"center": v(51797.56, -1472.23) * mm, "radius": 62.45 * mm});
            skArc(sketch, "E467", {"start": v(51797.56, -1396.03) * mm, "mid": v(51743.68, -1418.35) * mm, "end": v(51721.36, -1472.23) * mm});
            skCircle(sketch, "E468", {"center": v(51380.17, -1487.04) * mm, "radius": 6.35 * mm});
            skCircle(sketch, "E469", {"center": v(51353.06, -1472.23) * mm, "radius": 108.79 * mm});
            skArc(sketch, "E470", {"start": v(51340.22, -1349.43) * mm, "mid": v(51257.14, -1394.48) * mm, "end": v(51230.26, -1485.08) * mm});
            skLineSegment(sketch, "E471", {"start": v(51502, -1472.23) * mm, "end": v(51204.12, -1472.23) * mm});
            skLineSegment(sketch, "E472", {"start": v(51353.06, -1323.28) * mm, "end": v(51353.06, -1621.18) * mm});
            skLineSegment(sketch, "E473", {"start": v(52496.06, -1472.23) * mm, "end": v(50210.06, -1472.23) * mm});
            skLineSegment(sketch, "E474", {"start": v(51353.06, -2996.23) * mm, "end": v(51353.06, -2742.23) * mm});
            skLineSegment(sketch, "E475", {"start": v(51480.06, -2869.23) * mm, "end": v(51226.06, -2869.23) * mm});
            skCircle(sketch, "E476", {"center": v(51353.06, -2869.23) * mm, "radius": 62.45 * mm});
            skArc(sketch, "E477", {"start": v(51429.26, -2869.23) * mm, "mid": v(51406.95, -2815.35) * mm, "end": v(51353.06, -2793.03) * mm});
            skLineSegment(sketch, "E478", {"start": v(49956.06, -1599.23) * mm, "end": v(49956.06, -1345.23) * mm});
            skLineSegment(sketch, "E479", {"start": v(50083.06, -1472.23) * mm, "end": v(49829.06, -1472.23) * mm});
            skCircle(sketch, "E480", {"center": v(49956.06, -1472.23) * mm, "radius": 62.45 * mm});
            skArc(sketch, "E481", {"start": v(50032.26, -1472.23) * mm, "mid": v(50009.95, -1418.35) * mm, "end": v(49956.06, -1396.03) * mm});
            skLineSegment(sketch, "E482", {"start": v(51353.06, -202.23) * mm, "end": v(51353.06, 51.77) * mm});
            skLineSegment(sketch, "E483", {"start": v(51480.06, -75.23) * mm, "end": v(51226.06, -75.23) * mm});
            skCircle(sketch, "E484", {"center": v(51353.06, -75.23) * mm, "radius": 62.45 * mm});
            skArc(sketch, "E485", {"start": v(51429.26, -75.23) * mm, "mid": v(51406.95, -21.35) * mm, "end": v(51353.06, 0.97) * mm});
            skLineSegment(sketch, "E486", {"start": v(52750.06, -1599.23) * mm, "end": v(52750.06, -1345.23) * mm});
            skLineSegment(sketch, "E487", {"start": v(52877.06, -1472.23) * mm, "end": v(52623.06, -1472.23) * mm});
            skCircle(sketch, "E488", {"center": v(52750.06, -1472.23) * mm, "radius": 62.45 * mm});
            skArc(sketch, "E489", {"start": v(52826.26, -1472.23) * mm, "mid": v(52803.95, -1418.35) * mm, "end": v(52750.06, -1396.03) * mm});
            skCircle(sketch, "E490", {"center": v(37891.06, -1472.23) * mm, "radius": 1397 * mm});
            skLineSegment(sketch, "E491", {"start": v(36240.06, -1472.23) * mm, "end": v(39542.06, -1472.23) * mm});
            skLineSegment(sketch, "E492", {"start": v(37891.06, -3109.05) * mm, "end": v(37891.06, 192.95) * mm});
            skLineSegment(sketch, "E493", {"start": v(37891.06, -456.23) * mm, "end": v(37891.06, -2488.23) * mm});
            skLineSegment(sketch, "E494", {"start": v(36875.06, -1472.23) * mm, "end": v(38907.06, -1472.23) * mm});
            skCircle(sketch, "E495", {"center": v(37891.06, -1472.23) * mm, "radius": 444.5 * mm});
            skCircle(sketch, "E496", {"center": v(37413.13, -1453.96) * mm, "radius": 6.35 * mm});
            skLineSegment(sketch, "E497", {"start": v(37344.96, -1472.23) * mm, "end": v(37548.16, -1472.23) * mm});
            skLineSegment(sketch, "E498", {"start": v(37446.56, -1573.83) * mm, "end": v(37446.56, -1370.63) * mm});
            skCircle(sketch, "E499", {"center": v(37446.56, -1472.23) * mm, "radius": 62.45 * mm});
            skArc(sketch, "E500", {"start": v(37446.56, -1548.43) * mm, "mid": v(37500.45, -1526.11) * mm, "end": v(37522.76, -1472.23) * mm});
            skCircle(sketch, "E501", {"center": v(37872.8, -1950.17) * mm, "radius": 6.35 * mm});
            skLineSegment(sketch, "E502", {"start": v(37891.06, -2018.33) * mm, "end": v(37891.06, -1815.13) * mm});
            skLineSegment(sketch, "E503", {"start": v(37992.66, -1916.73) * mm, "end": v(37789.46, -1916.73) * mm});
            skCircle(sketch, "E504", {"center": v(37891.06, -1916.73) * mm, "radius": 62.45 * mm});
            skArc(sketch, "E505", {"start": v(37967.26, -1916.73) * mm, "mid": v(37944.95, -1862.85) * mm, "end": v(37891.06, -1840.53) * mm});
            skCircle(sketch, "E506", {"center": v(38369, -1490.5) * mm, "radius": 6.35 * mm});
            skLineSegment(sketch, "E507", {"start": v(38437.16, -1472.23) * mm, "end": v(38233.96, -1472.23) * mm});
            skLineSegment(sketch, "E508", {"start": v(38335.56, -1370.63) * mm, "end": v(38335.56, -1573.83) * mm});
            skCircle(sketch, "E509", {"center": v(38335.56, -1472.23) * mm, "radius": 62.45 * mm});
            skArc(sketch, "E510", {"start": v(38335.56, -1396.03) * mm, "mid": v(38281.68, -1418.35) * mm, "end": v(38259.36, -1472.23) * mm});
            skCircle(sketch, "E511", {"center": v(37909.33, -994.3) * mm, "radius": 6.35 * mm});
            skLineSegment(sketch, "E512", {"start": v(37891.06, -926.13) * mm, "end": v(37891.06, -1129.33) * mm});
            skLineSegment(sketch, "E513", {"start": v(37789.46, -1027.73) * mm, "end": v(37992.66, -1027.73) * mm});
            skCircle(sketch, "E514", {"center": v(37891.06, -1027.73) * mm, "radius": 62.45 * mm});
            skArc(sketch, "E515", {"start": v(37814.86, -1027.73) * mm, "mid": v(37837.18, -1081.61) * mm, "end": v(37891.06, -1103.93) * mm});
            skCircle(sketch, "E516", {"center": v(37905.87, -1445.12) * mm, "radius": 6.35 * mm});
            skCircle(sketch, "E517", {"center": v(37891.06, -1472.23) * mm, "radius": 108.79 * mm});
            skArc(sketch, "E518", {"start": v(37768.26, -1485.08) * mm, "mid": v(37813.31, -1568.15) * mm, "end": v(37903.91, -1595.03) * mm});
            skLineSegment(sketch, "E519", {"start": v(37891.06, -1323.28) * mm, "end": v(37891.06, -1621.18) * mm});
            skLineSegment(sketch, "E520", {"start": v(37742.12, -1472.23) * mm, "end": v(38040, -1472.23) * mm});
            skLineSegment(sketch, "E521", {"start": v(37891.06, -329.23) * mm, "end": v(37891.06, -2615.23) * mm});
            skLineSegment(sketch, "E522", {"start": v(39415.06, -1472.23) * mm, "end": v(39161.06, -1472.23) * mm});
            skLineSegment(sketch, "E523", {"start": v(39288.06, -1345.23) * mm, "end": v(39288.06, -1599.23) * mm});
            skCircle(sketch, "E524", {"center": v(39288.06, -1472.23) * mm, "radius": 62.45 * mm});
            skArc(sketch, "E525", {"start": v(39288.06, -1396.03) * mm, "mid": v(39234.18, -1418.35) * mm, "end": v(39211.86, -1472.23) * mm});
            skLineSegment(sketch, "E526", {"start": v(38018.06, -2869.23) * mm, "end": v(37764.06, -2869.23) * mm});
            skLineSegment(sketch, "E527", {"start": v(37891.06, -2742.23) * mm, "end": v(37891.06, -2996.23) * mm});
            skCircle(sketch, "E528", {"center": v(37891.06, -2869.23) * mm, "radius": 62.45 * mm});
            skArc(sketch, "E529", {"start": v(37891.06, -2793.03) * mm, "mid": v(37837.18, -2815.35) * mm, "end": v(37814.86, -2869.23) * mm});
            skLineSegment(sketch, "E530", {"start": v(36621.06, -1472.23) * mm, "end": v(36367.06, -1472.23) * mm});
            skLineSegment(sketch, "E531", {"start": v(36494.06, -1345.23) * mm, "end": v(36494.06, -1599.23) * mm});
            skCircle(sketch, "E532", {"center": v(36494.06, -1472.23) * mm, "radius": 62.45 * mm});
            skArc(sketch, "E533", {"start": v(36494.06, -1396.03) * mm, "mid": v(36440.18, -1418.35) * mm, "end": v(36417.86, -1472.23) * mm});
            skLineSegment(sketch, "E534", {"start": v(38018.06, -75.23) * mm, "end": v(37764.06, -75.23) * mm});
            skLineSegment(sketch, "E535", {"start": v(37891.06, 51.77) * mm, "end": v(37891.06, -202.23) * mm});
            skCircle(sketch, "E536", {"center": v(37891.06, -75.23) * mm, "radius": 62.45 * mm});
            skArc(sketch, "E537", {"start": v(37891.06, 0.97) * mm, "mid": v(37837.18, -21.35) * mm, "end": v(37814.86, -75.23) * mm});
            skLineSegment(sketch, "E538", {"start": v(37002.06, 178.77) * mm, "end": v(52242.06, 178.77) * mm});
            skLineSegment(sketch, "E539", {"start": v(53004.06, -2361.23) * mm, "end": v(53004.06, -583.23) * mm});
            skLineSegment(sketch, "E540", {"start": v(36240.06, -2361.23) * mm, "end": v(36240.06, -583.23) * mm});
            skLineSegment(sketch, "E541", {"start": v(37002.06, -3123.23) * mm, "end": v(41320.06, -3123.23) * mm});
            skLineSegment(sketch, "E542", {"start": v(53004.06, -2361.23) * mm, "end": v(52242.06, -3123.23) * mm});
            skLineSegment(sketch, "E543", {"start": v(53004.06, -583.23) * mm, "end": v(52242.06, 178.77) * mm});
            skLineSegment(sketch, "E544", {"start": v(37002.06, -3123.23) * mm, "end": v(36240.06, -2361.23) * mm});
            skLineSegment(sketch, "E545", {"start": v(37002.06, 178.77) * mm, "end": v(36240.06, -583.23) * mm});
            skLineSegment(sketch, "E546", {"start": v(47924.06, -3123.23) * mm, "end": v(52242.06, -3123.23) * mm});
            skLineSegment(sketch, "E547", {"start": v(44622.06, -8595.3) * mm, "end": v(44622.06, -35381.23) * mm});
            skCircle(sketch, "E548", {"center": v(51353.06, -33730.23) * mm, "radius": 1397 * mm});
            skLineSegment(sketch, "E549", {"start": v(51353.06, -35381.23) * mm, "end": v(51353.06, -32079.23) * mm});
            skLineSegment(sketch, "E550", {"start": v(49716.24, -33730.23) * mm, "end": v(53018.24, -33730.23) * mm});
            skLineSegment(sketch, "E551", {"start": v(52369.06, -33730.23) * mm, "end": v(50337.06, -33730.23) * mm});
            skLineSegment(sketch, "E552", {"start": v(51353.06, -34746.23) * mm, "end": v(51353.06, -32714.23) * mm});
            skCircle(sketch, "E553", {"center": v(51353.06, -33730.23) * mm, "radius": 444.5 * mm});
            skCircle(sketch, "E554", {"center": v(51371.33, -34208.17) * mm, "radius": 6.35 * mm});
            skLineSegment(sketch, "E555", {"start": v(51353.06, -34276.33) * mm, "end": v(51353.06, -34073.13) * mm});
            skLineSegment(sketch, "E556", {"start": v(51251.46, -34174.73) * mm, "end": v(51454.66, -34174.73) * mm});
            skCircle(sketch, "E557", {"center": v(51353.06, -34174.73) * mm, "radius": 62.45 * mm});
            skArc(sketch, "E558", {"start": v(51353.06, -34098.53) * mm, "mid": v(51299.18, -34120.85) * mm, "end": v(51276.86, -34174.73) * mm});
            skCircle(sketch, "E559", {"center": v(50875.13, -33748.5) * mm, "radius": 6.35 * mm});
            skLineSegment(sketch, "E560", {"start": v(50806.96, -33730.23) * mm, "end": v(51010.16, -33730.23) * mm});
            skLineSegment(sketch, "E561", {"start": v(50908.56, -33628.63) * mm, "end": v(50908.56, -33831.83) * mm});
            skCircle(sketch, "E562", {"center": v(50908.56, -33730.23) * mm, "radius": 62.45 * mm});
            skArc(sketch, "E563", {"start": v(50984.76, -33730.23) * mm, "mid": v(50962.45, -33676.35) * mm, "end": v(50908.56, -33654.03) * mm});
            skCircle(sketch, "E564", {"center": v(51334.8, -33252.3) * mm, "radius": 6.35 * mm});
            skLineSegment(sketch, "E565", {"start": v(51353.06, -33184.13) * mm, "end": v(51353.06, -33387.33) * mm});
            skLineSegment(sketch, "E566", {"start": v(51454.66, -33285.73) * mm, "end": v(51251.46, -33285.73) * mm});
            skCircle(sketch, "E567", {"center": v(51353.06, -33285.73) * mm, "radius": 62.45 * mm});
            skArc(sketch, "E568", {"start": v(51353.06, -33361.93) * mm, "mid": v(51406.95, -33339.61) * mm, "end": v(51429.26, -33285.73) * mm});
            skCircle(sketch, "E569", {"center": v(51831, -33711.96) * mm, "radius": 6.35 * mm});
            skLineSegment(sketch, "E570", {"start": v(51899.16, -33730.23) * mm, "end": v(51695.96, -33730.23) * mm});
            skLineSegment(sketch, "E571", {"start": v(51797.56, -33831.83) * mm, "end": v(51797.56, -33628.63) * mm});
            skCircle(sketch, "E572", {"center": v(51797.56, -33730.23) * mm, "radius": 62.45 * mm});
            skArc(sketch, "E573", {"start": v(51721.36, -33730.23) * mm, "mid": v(51743.68, -33784.11) * mm, "end": v(51797.56, -33806.43) * mm});
            skCircle(sketch, "E574", {"center": v(51380.17, -33715.42) * mm, "radius": 6.35 * mm});
            skCircle(sketch, "E575", {"center": v(51353.06, -33730.23) * mm, "radius": 108.79 * mm});
            skArc(sketch, "E576", {"start": v(51230.26, -33717.38) * mm, "mid": v(51257.14, -33807.98) * mm, "end": v(51340.22, -33853.03) * mm});
            skLineSegment(sketch, "E577", {"start": v(51502, -33730.23) * mm, "end": v(51204.12, -33730.23) * mm});
            skLineSegment(sketch, "E578", {"start": v(51353.06, -33879.18) * mm, "end": v(51353.06, -33581.28) * mm});
            skLineSegment(sketch, "E579", {"start": v(52496.06, -33730.23) * mm, "end": v(50210.06, -33730.23) * mm});
            skLineSegment(sketch, "E580", {"start": v(51353.06, -32206.23) * mm, "end": v(51353.06, -32460.23) * mm});
            skLineSegment(sketch, "E581", {"start": v(51480.06, -32333.23) * mm, "end": v(51226.06, -32333.23) * mm});
            skCircle(sketch, "E582", {"center": v(51353.06, -32333.23) * mm, "radius": 62.45 * mm});
            skArc(sketch, "E583", {"start": v(51353.06, -32409.43) * mm, "mid": v(51406.95, -32387.11) * mm, "end": v(51429.26, -32333.23) * mm});
            skLineSegment(sketch, "E584", {"start": v(49956.06, -33603.23) * mm, "end": v(49956.06, -33857.23) * mm});
            skLineSegment(sketch, "E585", {"start": v(50083.06, -33730.23) * mm, "end": v(49829.06, -33730.23) * mm});
            skCircle(sketch, "E586", {"center": v(49956.06, -33730.23) * mm, "radius": 62.45 * mm});
            skArc(sketch, "E587", {"start": v(49956.06, -33806.43) * mm, "mid": v(50009.95, -33784.11) * mm, "end": v(50032.26, -33730.23) * mm});
            skLineSegment(sketch, "E588", {"start": v(51353.06, -35000.23) * mm, "end": v(51353.06, -35254.23) * mm});
            skLineSegment(sketch, "E589", {"start": v(51480.06, -35127.23) * mm, "end": v(51226.06, -35127.23) * mm});
            skCircle(sketch, "E590", {"center": v(51353.06, -35127.23) * mm, "radius": 62.45 * mm});
            skArc(sketch, "E591", {"start": v(51353.06, -35203.43) * mm, "mid": v(51406.95, -35181.11) * mm, "end": v(51429.26, -35127.23) * mm});
            skLineSegment(sketch, "E592", {"start": v(52750.06, -33603.23) * mm, "end": v(52750.06, -33857.23) * mm});
            skLineSegment(sketch, "E593", {"start": v(52877.06, -33730.23) * mm, "end": v(52623.06, -33730.23) * mm});
            skCircle(sketch, "E594", {"center": v(52750.06, -33730.23) * mm, "radius": 62.45 * mm});
            skArc(sketch, "E595", {"start": v(52750.06, -33806.43) * mm, "mid": v(52803.95, -33784.11) * mm, "end": v(52826.26, -33730.23) * mm});
            skCircle(sketch, "E596", {"center": v(37891.06, -33730.23) * mm, "radius": 1397 * mm});
            skLineSegment(sketch, "E597", {"start": v(36240.06, -33730.23) * mm, "end": v(39542.06, -33730.23) * mm});
            skLineSegment(sketch, "E598", {"start": v(7613.78, -5028.23) * mm, "end": v(7613.78, -30174.23) * mm});
            skLineSegment(sketch, "E599", {"start": v(7613.78, -30174.23) * mm, "end": v(-42475.02, -30174.23) * mm});
            skLineSegment(sketch, "E600", {"start": v(-42475.02, -30174.23) * mm, "end": v(-42475.02, -5028.23) * mm});
            skLineSegment(sketch, "E601", {"start": v(-42475.02, -5028.23) * mm, "end": v(7613.78, -5028.23) * mm});
            skCircle(sketch, "E602", {"center": v(-17430.62, -17601.23) * mm, "radius": 28023.25 * mm});
            skLineSegment(sketch, "E603", {"start": v(-53625.62, 178.77) * mm, "end": v(18764.38, 178.77) * mm});
            skLineSegment(sketch, "E604", {"start": v(-52609.62, -329.23) * mm, "end": v(17748.38, -329.23) * mm});
            skLineSegment(sketch, "E605", {"start": v(-52609.62, -434.64) * mm, "end": v(17748.38, -434.64) * mm});
            skLineSegment(sketch, "E606", {"start": v(-52609.62, -223.82) * mm, "end": v(17748.38, -223.82) * mm});
            skLineSegment(sketch, "E607", {"start": v(-52609.62, -837.23) * mm, "end": v(17748.38, -837.23) * mm});
            skLineSegment(sketch, "E608", {"start": v(18764.38, 178.77) * mm, "end": v(18764.38, -6425.23) * mm});
            skLineSegment(sketch, "E609", {"start": v(18256.38, 178.77) * mm, "end": v(18256.38, -6425.23) * mm});
            skLineSegment(sketch, "E610", {"start": v(18150.97, 178.77) * mm, "end": v(18150.97, -6425.23) * mm});
            skLineSegment(sketch, "E611", {"start": v(18361.79, 178.77) * mm, "end": v(18361.79, -6425.23) * mm});
            skLineSegment(sketch, "E612", {"start": v(17748.38, 178.77) * mm, "end": v(17748.38, -6425.23) * mm});
            skLineSegment(sketch, "E613", {"start": v(-53625.62, 178.77) * mm, "end": v(-53625.62, -6425.23) * mm});
            skLineSegment(sketch, "E614", {"start": v(-53117.62, 178.77) * mm, "end": v(-53117.62, -6425.23) * mm});
            skLineSegment(sketch, "E615", {"start": v(-53012.21, 178.77) * mm, "end": v(-53012.21, -6425.23) * mm});
            skLineSegment(sketch, "E616", {"start": v(-53223.03, 178.77) * mm, "end": v(-53223.03, -6425.23) * mm});
            skLineSegment(sketch, "E617", {"start": v(-52609.62, 178.77) * mm, "end": v(-52609.62, -6425.23) * mm});
            skLineSegment(sketch, "E618", {"start": v(-52609.62, -5409.23) * mm, "end": v(17748.38, -5409.23) * mm});
            skLineSegment(sketch, "E619", {"start": v(-52609.62, -5917.23) * mm, "end": v(17748.38, -5917.23) * mm});
            skLineSegment(sketch, "E620", {"start": v(-52609.62, -6022.64) * mm, "end": v(17748.38, -6022.64) * mm});
            skLineSegment(sketch, "E621", {"start": v(-52609.62, -5811.82) * mm, "end": v(17748.38, -5811.82) * mm});
            skLineSegment(sketch, "E622", {"start": v(-53625.62, -6425.23) * mm, "end": v(18764.38, -6425.23) * mm});
            skLineSegment(sketch, "E623", {"start": v(-36480.62, 42322.48) * mm, "end": v(1619.38, 42322.48) * mm});
            skLineSegment(sketch, "E624", {"start": v(1619.38, 42322.48) * mm, "end": v(1619.38, 45624.48) * mm});
            skLineSegment(sketch, "E625", {"start": v(349.38, 43465.48) * mm, "end": v(349.38, 44481.48) * mm});
            skLineSegment(sketch, "E626", {"start": v(-158.62, 43465.48) * mm, "end": v(-158.62, 44481.48) * mm});
            skLineSegment(sketch, "E627", {"start": v(1619.38, 45624.48) * mm, "end": v(-36480.62, 45624.48) * mm});
            skLineSegment(sketch, "E628", {"start": v(-36480.62, 45624.48) * mm, "end": v(-36480.62, 42322.48) * mm});
            skLineSegment(sketch, "E629", {"start": v(-35210.62, 44481.48) * mm, "end": v(-35210.62, 43465.48) * mm});
            skLineSegment(sketch, "E630", {"start": v(-34702.62, 44481.48) * mm, "end": v(-34702.62, 43465.48) * mm});
            skLineSegment(sketch, "E631", {"start": v(-35210.62, 44481.48) * mm, "end": v(349.38, 44481.48) * mm});
            skLineSegment(sketch, "E632", {"start": v(-35210.62, 43465.48) * mm, "end": v(349.38, 43465.48) * mm});
            skLineSegment(sketch, "E633", {"start": v(-36480.62, 34829.48) * mm, "end": v(1619.38, 34829.48) * mm});
            skLineSegment(sketch, "E634", {"start": v(1619.38, 34829.48) * mm, "end": v(1619.38, 38131.48) * mm});
            skLineSegment(sketch, "E635", {"start": v(349.38, 35972.48) * mm, "end": v(349.38, 36988.48) * mm});
            skLineSegment(sketch, "E636", {"start": v(-158.62, 35972.48) * mm, "end": v(-158.62, 36988.48) * mm});
            skLineSegment(sketch, "E637", {"start": v(1619.38, 38131.48) * mm, "end": v(-36480.62, 38131.48) * mm});
            skLineSegment(sketch, "E638", {"start": v(-36480.62, 38131.48) * mm, "end": v(-36480.62, 34829.48) * mm});
            skLineSegment(sketch, "E639", {"start": v(-35210.62, 36988.48) * mm, "end": v(-35210.62, 35972.48) * mm});
            skLineSegment(sketch, "E640", {"start": v(-34702.62, 36988.48) * mm, "end": v(-34702.62, 35972.48) * mm});
            skLineSegment(sketch, "E641", {"start": v(-35210.62, 36988.48) * mm, "end": v(349.38, 36988.48) * mm});
            skLineSegment(sketch, "E642", {"start": v(-35210.62, 35972.48) * mm, "end": v(349.38, 35972.48) * mm});
            skLineSegment(sketch, "E643", {"start": v(-36480.62, 20859.48) * mm, "end": v(1619.38, 20859.48) * mm});
            skLineSegment(sketch, "E644", {"start": v(1619.38, 20859.48) * mm, "end": v(1619.38, 24161.48) * mm});
            skLineSegment(sketch, "E645", {"start": v(349.38, 22002.48) * mm, "end": v(349.38, 23018.48) * mm});
            skLineSegment(sketch, "E646", {"start": v(-158.62, 22002.48) * mm, "end": v(-158.62, 23018.48) * mm});
            skLineSegment(sketch, "E647", {"start": v(1619.38, 24161.48) * mm, "end": v(-36480.62, 24161.48) * mm});
            skLineSegment(sketch, "E648", {"start": v(-36480.62, 24161.48) * mm, "end": v(-36480.62, 20859.48) * mm});
            skLineSegment(sketch, "E649", {"start": v(-35210.62, 23018.48) * mm, "end": v(-35210.62, 22002.48) * mm});
            skLineSegment(sketch, "E650", {"start": v(-34702.62, 23018.48) * mm, "end": v(-34702.62, 22002.48) * mm});
            skLineSegment(sketch, "E651", {"start": v(-35210.62, 23018.48) * mm, "end": v(349.38, 23018.48) * mm});
            skLineSegment(sketch, "E652", {"start": v(-35210.62, 22002.48) * mm, "end": v(349.38, 22002.48) * mm});
            skLineSegment(sketch, "E653", {"start": v(-52228.62, -33730.23) * mm, "end": v(-18700.62, -33730.23) * mm});
            skLineSegment(sketch, "E654", {"start": v(-18700.62, -33730.23) * mm, "end": v(-18700.62, -30428.23) * mm});
            skLineSegment(sketch, "E655", {"start": v(-19970.62, -32587.23) * mm, "end": v(-19970.62, -31571.23) * mm});
            skLineSegment(sketch, "E656", {"start": v(-20478.62, -32587.23) * mm, "end": v(-20478.62, -31571.23) * mm});
            skLineSegment(sketch, "E657", {"start": v(-18700.62, -30428.23) * mm, "end": v(-52228.62, -30428.23) * mm});
            skLineSegment(sketch, "E658", {"start": v(-52228.62, -30428.23) * mm, "end": v(-52228.62, -33730.23) * mm});
            skLineSegment(sketch, "E659", {"start": v(-50958.62, -31571.23) * mm, "end": v(-50958.62, -32587.23) * mm});
            skLineSegment(sketch, "E660", {"start": v(-50450.62, -31571.23) * mm, "end": v(-50450.62, -32587.23) * mm});
            skLineSegment(sketch, "E661", {"start": v(-50958.62, -31571.23) * mm, "end": v(-19970.62, -31571.23) * mm});
            skLineSegment(sketch, "E662", {"start": v(-50958.62, -32587.23) * mm, "end": v(-19970.62, -32587.23) * mm});
            skLineSegment(sketch, "E663", {"start": v(-52228.62, -26237.23) * mm, "end": v(-18700.62, -26237.23) * mm});
            skLineSegment(sketch, "E664", {"start": v(-18700.62, -26237.23) * mm, "end": v(-18700.62, -22935.23) * mm});
            skLineSegment(sketch, "E665", {"start": v(-19970.62, -25094.23) * mm, "end": v(-19970.62, -24078.23) * mm});
            skLineSegment(sketch, "E666", {"start": v(-20478.62, -25094.23) * mm, "end": v(-20478.62, -24078.23) * mm});
            skLineSegment(sketch, "E667", {"start": v(-18700.62, -22935.23) * mm, "end": v(-52228.62, -22935.23) * mm});
            skLineSegment(sketch, "E668", {"start": v(-52228.62, -22935.23) * mm, "end": v(-52228.62, -26237.23) * mm});
            skLineSegment(sketch, "E669", {"start": v(-50958.62, -24078.23) * mm, "end": v(-50958.62, -25094.23) * mm});
            skLineSegment(sketch, "E670", {"start": v(-50450.62, -24078.23) * mm, "end": v(-50450.62, -25094.23) * mm});
            skLineSegment(sketch, "E671", {"start": v(-50958.62, -24078.23) * mm, "end": v(-19970.62, -24078.23) * mm});
            skLineSegment(sketch, "E672", {"start": v(-50958.62, -25094.23) * mm, "end": v(-19970.62, -25094.23) * mm});
            skLineSegment(sketch, "E673", {"start": v(-52228.62, -12267.23) * mm, "end": v(-18700.62, -12267.23) * mm});
            skLineSegment(sketch, "E674", {"start": v(-18700.62, -12267.23) * mm, "end": v(-18700.62, -8965.23) * mm});
            skLineSegment(sketch, "E675", {"start": v(-19970.62, -11124.23) * mm, "end": v(-19970.62, -10108.23) * mm});
            skLineSegment(sketch, "E676", {"start": v(-20478.62, -11124.23) * mm, "end": v(-20478.62, -10108.23) * mm});
            skLineSegment(sketch, "E677", {"start": v(-18700.62, -8965.23) * mm, "end": v(-52228.62, -8965.23) * mm});
            skLineSegment(sketch, "E678", {"start": v(-52228.62, -8965.23) * mm, "end": v(-52228.62, -12267.23) * mm});
            skLineSegment(sketch, "E679", {"start": v(-50958.62, -10108.23) * mm, "end": v(-50958.62, -11124.23) * mm});
            skLineSegment(sketch, "E680", {"start": v(-50450.62, -10108.23) * mm, "end": v(-50450.62, -11124.23) * mm});
            skLineSegment(sketch, "E681", {"start": v(-50958.62, -10108.23) * mm, "end": v(-19970.62, -10108.23) * mm});
            skLineSegment(sketch, "E682", {"start": v(-50958.62, -11124.23) * mm, "end": v(-19970.62, -11124.23) * mm});
            skLineSegment(sketch, "E683", {"start": v(-52228.62, -4774.23) * mm, "end": v(-18700.62, -4774.23) * mm});
            skLineSegment(sketch, "E684", {"start": v(-18700.62, -4774.23) * mm, "end": v(-18700.62, -1472.23) * mm});
            skLineSegment(sketch, "E685", {"start": v(-19970.62, -3631.23) * mm, "end": v(-19970.62, -2615.23) * mm});
            skLineSegment(sketch, "E686", {"start": v(-20478.62, -3631.23) * mm, "end": v(-20478.62, -2615.23) * mm});
            skLineSegment(sketch, "E687", {"start": v(-18700.62, -1472.23) * mm, "end": v(-52228.62, -1472.23) * mm});
            skLineSegment(sketch, "E688", {"start": v(-52228.62, -1472.23) * mm, "end": v(-52228.62, -4774.23) * mm});
            skLineSegment(sketch, "E689", {"start": v(-50958.62, -2615.23) * mm, "end": v(-50958.62, -3631.23) * mm});
            skLineSegment(sketch, "E690", {"start": v(-50450.62, -2615.23) * mm, "end": v(-50450.62, -3631.23) * mm});
            skLineSegment(sketch, "E691", {"start": v(-50958.62, -2615.23) * mm, "end": v(-19970.62, -2615.23) * mm});
            skLineSegment(sketch, "E692", {"start": v(-50958.62, -3631.23) * mm, "end": v(-19970.62, -3631.23) * mm});
            skLineSegment(sketch, "E693", {"start": v(-16160.62, -33730.23) * mm, "end": v(17367.38, -33730.23) * mm});
            skLineSegment(sketch, "E694", {"start": v(17367.38, -33730.23) * mm, "end": v(17367.38, -30428.23) * mm});
            skLineSegment(sketch, "E695", {"start": v(16097.38, -32587.23) * mm, "end": v(16097.38, -31571.23) * mm});
            skLineSegment(sketch, "E696", {"start": v(15589.38, -32587.23) * mm, "end": v(15589.38, -31571.23) * mm});
            skLineSegment(sketch, "E697", {"start": v(17367.38, -30428.23) * mm, "end": v(-16160.62, -30428.23) * mm});
            skLineSegment(sketch, "E698", {"start": v(-16160.62, -30428.23) * mm, "end": v(-16160.62, -33730.23) * mm});
            skLineSegment(sketch, "E699", {"start": v(-14890.62, -31571.23) * mm, "end": v(-14890.62, -32587.23) * mm});
            skLineSegment(sketch, "E700", {"start": v(-14382.62, -31571.23) * mm, "end": v(-14382.62, -32587.23) * mm});
            skLineSegment(sketch, "E701", {"start": v(-14890.62, -31571.23) * mm, "end": v(16097.38, -31571.23) * mm});
            skLineSegment(sketch, "E702", {"start": v(-14890.62, -32587.23) * mm, "end": v(16097.38, -32587.23) * mm});
            skLineSegment(sketch, "E703", {"start": v(-16160.62, -26237.23) * mm, "end": v(17367.38, -26237.23) * mm});
            skLineSegment(sketch, "E704", {"start": v(17367.38, -26237.23) * mm, "end": v(17367.38, -22935.23) * mm});
            skLineSegment(sketch, "E705", {"start": v(16097.38, -25094.23) * mm, "end": v(16097.38, -24078.23) * mm});
            skLineSegment(sketch, "E706", {"start": v(15589.38, -25094.23) * mm, "end": v(15589.38, -24078.23) * mm});
            skLineSegment(sketch, "E707", {"start": v(17367.38, -22935.23) * mm, "end": v(-16160.62, -22935.23) * mm});
            skLineSegment(sketch, "E708", {"start": v(-16160.62, -22935.23) * mm, "end": v(-16160.62, -26237.23) * mm});
            skLineSegment(sketch, "E709", {"start": v(-14890.62, -24078.23) * mm, "end": v(-14890.62, -25094.23) * mm});
            skLineSegment(sketch, "E710", {"start": v(-14382.62, -24078.23) * mm, "end": v(-14382.62, -25094.23) * mm});
            skLineSegment(sketch, "E711", {"start": v(-14890.62, -24078.23) * mm, "end": v(16097.38, -24078.23) * mm});
            skLineSegment(sketch, "E712", {"start": v(-14890.62, -25094.23) * mm, "end": v(16097.38, -25094.23) * mm});
            skLineSegment(sketch, "E713", {"start": v(-16160.62, -12267.23) * mm, "end": v(17367.38, -12267.23) * mm});
            skLineSegment(sketch, "E714", {"start": v(17367.38, -12267.23) * mm, "end": v(17367.38, -8965.23) * mm});
            skLineSegment(sketch, "E715", {"start": v(16097.38, -11124.23) * mm, "end": v(16097.38, -10108.23) * mm});
            skLineSegment(sketch, "E716", {"start": v(15589.38, -11124.23) * mm, "end": v(15589.38, -10108.23) * mm});
            skLineSegment(sketch, "E717", {"start": v(17367.38, -8965.23) * mm, "end": v(-16160.62, -8965.23) * mm});
            skLineSegment(sketch, "E718", {"start": v(-16160.62, -8965.23) * mm, "end": v(-16160.62, -12267.23) * mm});
            skLineSegment(sketch, "E719", {"start": v(-14890.62, -10108.23) * mm, "end": v(-14890.62, -11124.23) * mm});
            skLineSegment(sketch, "E720", {"start": v(-14382.62, -10108.23) * mm, "end": v(-14382.62, -11124.23) * mm});
            skLineSegment(sketch, "E721", {"start": v(-14890.62, -10108.23) * mm, "end": v(16097.38, -10108.23) * mm});
            skLineSegment(sketch, "E722", {"start": v(-14890.62, -11124.23) * mm, "end": v(16097.38, -11124.23) * mm});
            skLineSegment(sketch, "E723", {"start": v(-16160.62, -4774.23) * mm, "end": v(17367.38, -4774.23) * mm});
            skLineSegment(sketch, "E724", {"start": v(17367.38, -4774.23) * mm, "end": v(17367.38, -1472.23) * mm});
            skLineSegment(sketch, "E725", {"start": v(16097.38, -3631.23) * mm, "end": v(16097.38, -2615.23) * mm});
            skLineSegment(sketch, "E726", {"start": v(15589.38, -3631.23) * mm, "end": v(15589.38, -2615.23) * mm});
            skLineSegment(sketch, "E727", {"start": v(17367.38, -1472.23) * mm, "end": v(-16160.62, -1472.23) * mm});
            skLineSegment(sketch, "E728", {"start": v(-16160.62, -1472.23) * mm, "end": v(-16160.62, -4774.23) * mm});
            skLineSegment(sketch, "E729", {"start": v(-14890.62, -2615.23) * mm, "end": v(-14890.62, -3631.23) * mm});
            skLineSegment(sketch, "E730", {"start": v(-14382.62, -2615.23) * mm, "end": v(-14382.62, -3631.23) * mm});
            skLineSegment(sketch, "E731", {"start": v(-14890.62, -2615.23) * mm, "end": v(16097.38, -2615.23) * mm});
            skLineSegment(sketch, "E732", {"start": v(-14890.62, -3631.23) * mm, "end": v(16097.38, -3631.23) * mm});
            skSolve(sketch);
        }
        {
            var Q0;
            Q0=qCreatedBy(makeId("Top.planeOp"),FACE);
            var sketch = newSketch(context, id + "F1", { "sketchPlane" : qUnion([Q0])});
            skArc(sketch, "E733", {"start": v(41316.15, -9212.13) * mm, "mid": v(41854.3, -8990.37) * mm, "end": v(42079.99, -8453.85) * mm});
            skArc(sketch, "E734", {"start": v(47160.62, -8461.36) * mm, "mid": v(47385.73, -8994.85) * mm, "end": v(47921.53, -9214.39) * mm});
            skArc(sketch, "E735", {"start": v(47923.48, -25981.14) * mm, "mid": v(47384.14, -26205.24) * mm, "end": v(47161.28, -26745.1) * mm});
            skArc(sketch, "E736", {"start": v(42082.18, -26744.8) * mm, "mid": v(41859.73, -26205.92) * mm, "end": v(41321.78, -25981.26) * mm});
            skArc(sketch, "E737", {"start": v(41323.31, -32079.12) * mm, "mid": v(41858.79, -31853.91) * mm, "end": v(42078.74, -31316.26) * mm});
            skArc(sketch, "E738", {"start": v(47157.12, -31316.99) * mm, "mid": v(47384.84, -31856.7) * mm, "end": v(47927.14, -32078.15) * mm});
            skCircle(sketch, "E739", {"center": v(51353.18, -33283.9) * mm, "radius": 63.12 * mm});
            skCircle(sketch, "E740", {"center": v(50908.27, -33729.38) * mm, "radius": 63.14 * mm});
            skCircle(sketch, "E741", {"center": v(51797.97, -33729.38) * mm, "radius": 63.66 * mm});
            skCircle(sketch, "E742", {"center": v(51353.4, -34175.71) * mm, "radius": 62.1 * mm});
            skCircle(sketch, "E743", {"center": v(51352.58, -33729.9) * mm, "radius": 108.51 * mm});
            skCircle(sketch, "E744", {"center": v(52750.36, -33730.64) * mm, "radius": 63.37 * mm});
            skCircle(sketch, "E745", {"center": v(51353.01, -35127.3) * mm, "radius": 63.37 * mm});
            skCircle(sketch, "E746", {"center": v(49956.27, -33730.13) * mm, "radius": 63.37 * mm});
            skCircle(sketch, "E747", {"center": v(51352.9, -32333.07) * mm, "radius": 63.37 * mm});
            skCircle(sketch, "E748", {"center": v(37891.94, -33283.91) * mm, "radius": 63.12 * mm});
            skCircle(sketch, "E749", {"center": v(37447.04, -33729.39) * mm, "radius": 63.14 * mm});
            skCircle(sketch, "E750", {"center": v(38336.74, -33729.39) * mm, "radius": 63.66 * mm});
            skCircle(sketch, "E751", {"center": v(37892.17, -34175.72) * mm, "radius": 62.1 * mm});
            skCircle(sketch, "E752", {"center": v(37891.35, -33729.9) * mm, "radius": 108.51 * mm});
            skCircle(sketch, "E753", {"center": v(39289.13, -33730.65) * mm, "radius": 63.37 * mm});
            skCircle(sketch, "E754", {"center": v(37891.78, -35127.3) * mm, "radius": 63.37 * mm});
            skCircle(sketch, "E755", {"center": v(36495.03, -33730.13) * mm, "radius": 63.37 * mm});
            skCircle(sketch, "E756", {"center": v(37891.67, -32333.07) * mm, "radius": 63.37 * mm});
            skCircle(sketch, "E757", {"center": v(37891.36, -23886.17) * mm, "radius": 63.12 * mm});
            skCircle(sketch, "E758", {"center": v(37446.46, -24331.64) * mm, "radius": 63.14 * mm});
            skCircle(sketch, "E759", {"center": v(38336.16, -24331.64) * mm, "radius": 63.66 * mm});
            skCircle(sketch, "E760", {"center": v(37891.6, -24777.97) * mm, "radius": 62.1 * mm});
            skCircle(sketch, "E761", {"center": v(37890.77, -24332.15) * mm, "radius": 108.51 * mm});
            skCircle(sketch, "E762", {"center": v(39288.55, -24332.9) * mm, "radius": 63.37 * mm});
            skCircle(sketch, "E763", {"center": v(37891.2, -25729.56) * mm, "radius": 63.37 * mm});
            skCircle(sketch, "E764", {"center": v(36494.45, -24332.39) * mm, "radius": 63.37 * mm});
            skCircle(sketch, "E765", {"center": v(37891.1, -22935.33) * mm, "radius": 63.37 * mm});
            skCircle(sketch, "E766", {"center": v(37891.81, -10424.18) * mm, "radius": 63.12 * mm});
            skCircle(sketch, "E767", {"center": v(37446.9, -10869.65) * mm, "radius": 63.14 * mm});
            skCircle(sketch, "E768", {"center": v(38336.6, -10869.65) * mm, "radius": 63.66 * mm});
            skCircle(sketch, "E769", {"center": v(37892.04, -11315.98) * mm, "radius": 62.1 * mm});
            skCircle(sketch, "E770", {"center": v(37891.22, -10870.16) * mm, "radius": 108.51 * mm});
            skCircle(sketch, "E771", {"center": v(39289, -10870.92) * mm, "radius": 63.37 * mm});
            skCircle(sketch, "E772", {"center": v(37891.65, -12267.57) * mm, "radius": 63.37 * mm});
            skCircle(sketch, "E773", {"center": v(36494.9, -10870.4) * mm, "radius": 63.37 * mm});
            skCircle(sketch, "E774", {"center": v(37891.54, -9473.34) * mm, "radius": 63.37 * mm});
            skCircle(sketch, "E775", {"center": v(51353.8, -23886.1) * mm, "radius": 63.12 * mm});
            skCircle(sketch, "E776", {"center": v(50908.89, -24331.58) * mm, "radius": 63.14 * mm});
            skCircle(sketch, "E777", {"center": v(51798.58, -24331.58) * mm, "radius": 63.66 * mm});
            skCircle(sketch, "E778", {"center": v(51354.02, -24777.91) * mm, "radius": 62.1 * mm});
            skCircle(sketch, "E779", {"center": v(51353.2, -24332.1) * mm, "radius": 108.51 * mm});
            skCircle(sketch, "E780", {"center": v(52750.98, -24332.84) * mm, "radius": 63.37 * mm});
            skCircle(sketch, "E781", {"center": v(51353.63, -25729.5) * mm, "radius": 63.37 * mm});
            skCircle(sketch, "E782", {"center": v(49956.88, -24332.32) * mm, "radius": 63.37 * mm});
            skCircle(sketch, "E783", {"center": v(51353.52, -22935.26) * mm, "radius": 63.37 * mm});
            skCircle(sketch, "E784", {"center": v(51353.88, -10424.04) * mm, "radius": 63.12 * mm});
            skCircle(sketch, "E785", {"center": v(50908.97, -10869.51) * mm, "radius": 63.14 * mm});
            skCircle(sketch, "E786", {"center": v(51798.67, -10869.51) * mm, "radius": 63.66 * mm});
            skCircle(sketch, "E787", {"center": v(51354.11, -11315.84) * mm, "radius": 62.1 * mm});
            skCircle(sketch, "E788", {"center": v(51353.29, -10870.02) * mm, "radius": 108.51 * mm});
            skCircle(sketch, "E789", {"center": v(52751.06, -10870.77) * mm, "radius": 63.37 * mm});
            skCircle(sketch, "E790", {"center": v(51353.71, -12267.43) * mm, "radius": 63.37 * mm});
            skCircle(sketch, "E791", {"center": v(49956.97, -10870.25) * mm, "radius": 63.37 * mm});
            skCircle(sketch, "E792", {"center": v(51353.61, -9473.2) * mm, "radius": 63.37 * mm});
            skCircle(sketch, "E793", {"center": v(51353.65, -1026.27) * mm, "radius": 63.12 * mm});
            skCircle(sketch, "E794", {"center": v(50908.75, -1471.74) * mm, "radius": 63.14 * mm});
            skCircle(sketch, "E795", {"center": v(51798.44, -1471.74) * mm, "radius": 63.66 * mm});
            skCircle(sketch, "E796", {"center": v(51353.88, -1918.07) * mm, "radius": 62.1 * mm});
            skCircle(sketch, "E797", {"center": v(51353.06, -1472.25) * mm, "radius": 108.51 * mm});
            skCircle(sketch, "E798", {"center": v(52750.84, -1473) * mm, "radius": 63.37 * mm});
            skCircle(sketch, "E799", {"center": v(51353.49, -2869.66) * mm, "radius": 63.37 * mm});
            skCircle(sketch, "E800", {"center": v(49956.74, -1472.48) * mm, "radius": 63.37 * mm});
            skCircle(sketch, "E801", {"center": v(51353.38, -75.42) * mm, "radius": 63.37 * mm});
            skCircle(sketch, "E802", {"center": v(37891.68, -1026.2) * mm, "radius": 63.12 * mm});
            skCircle(sketch, "E803", {"center": v(37446.78, -1471.67) * mm, "radius": 63.14 * mm});
            skCircle(sketch, "E804", {"center": v(38336.48, -1471.67) * mm, "radius": 63.66 * mm});
            skCircle(sketch, "E805", {"center": v(37891.91, -1918) * mm, "radius": 62.1 * mm});
            skCircle(sketch, "E806", {"center": v(37891.1, -1472.18) * mm, "radius": 108.51 * mm});
            skCircle(sketch, "E807", {"center": v(39288.87, -1472.94) * mm, "radius": 63.37 * mm});
            skCircle(sketch, "E808", {"center": v(37891.52, -2869.6) * mm, "radius": 63.37 * mm});
            skCircle(sketch, "E809", {"center": v(36494.77, -1472.42) * mm, "radius": 63.37 * mm});
            skCircle(sketch, "E810", {"center": v(37891.42, -75.36) * mm, "radius": 63.37 * mm});
            skCircle(sketch, "E811", {"center": v(42907.4, -14631.43) * mm, "radius": 114.93 * mm});
            skCircle(sketch, "E812", {"center": v(46336.56, -14631.55) * mm, "radius": 114.93 * mm});
            skCircle(sketch, "E813", {"center": v(48051.08, -17601.27) * mm, "radius": 114.93 * mm});
            skCircle(sketch, "E814", {"center": v(46336.41, -20570.53) * mm, "radius": 114.93 * mm});
            skCircle(sketch, "E815", {"center": v(42907.6, -20570.8) * mm, "radius": 114.93 * mm});
            skCircle(sketch, "E816", {"center": v(41193.1, -17601.1) * mm, "radius": 114.93 * mm});
            skArc(sketch, "E817", {"start": v(36999.88, -32083.6) * mm, "mid": v(36452.92, -32289.56) * mm, "end": v(36240.05, -32833.86) * mm});
            skArc(sketch, "E818", {"start": v(36238.45, -34615.4) * mm, "mid": v(36491.56, -35125.51) * mm, "end": v(37000.6, -35380.75) * mm});
            skArc(sketch, "E819", {"start": v(36240.25, -25222.08) * mm, "mid": v(36510.92, -25712.29) * mm, "end": v(37002.14, -25981.13) * mm});
            skArc(sketch, "E820", {"start": v(36999.9, -9217.34) * mm, "mid": v(36486.07, -9464.21) * mm, "end": v(36239.33, -9978.11) * mm});
            skArc(sketch, "E821", {"start": v(42081.94, -3885.17) * mm, "mid": v(41857.55, -3346.3) * mm, "end": v(41317.73, -3124.22) * mm});
            skArc(sketch, "E822", {"start": v(36239.34, -2362.8) * mm, "mid": v(36471.84, -2893.08) * mm, "end": v(37002.98, -3123.62) * mm});
            skArc(sketch, "E823", {"start": v(37001.27, 179.29) * mm, "mid": v(36481.44, -62.35) * mm, "end": v(36239.55, -582.06) * mm});
            skArc(sketch, "E824", {"start": v(53004.05, -583.24) * mm, "mid": v(52760.98, -62) * mm, "end": v(52239.62, 180.82) * mm});
            skArc(sketch, "E825", {"start": v(52242.01, -3123.24) * mm, "mid": v(52797.16, -2916.57) * mm, "end": v(53003.86, -2361.44) * mm});
            skArc(sketch, "E826", {"start": v(47923.59, -3121.86) * mm, "mid": v(47384.26, -3349.13) * mm, "end": v(47163.08, -3891) * mm});
            skArc(sketch, "E827", {"start": v(53009.1, -9978.39) * mm, "mid": v(52747.8, -9472.75) * mm, "end": v(52239.4, -9216.86) * mm});
            skArc(sketch, "E828", {"start": v(52242.61, -25982.56) * mm, "mid": v(52761.86, -25740.23) * mm, "end": v(53004.06, -25220.93) * mm});
            skArc(sketch, "E829", {"start": v(53004.85, -32837.3) * mm, "mid": v(52731.37, -32349.92) * mm, "end": v(52244.25, -32076) * mm});
            skArc(sketch, "E830", {"start": v(52242.4, -35381.61) * mm, "mid": v(52761.77, -35136.87) * mm, "end": v(53004.25, -34616.45) * mm});
            skLineSegment(sketch, "E831", {"start": v(36238.45, -34615.4) * mm, "end": v(36240.05, -32833.86) * mm});
            skLineSegment(sketch, "E832", {"start": v(37000.6, -35380.75) * mm, "end": v(47748.82, -35390.44) * mm});
            skLineSegment(sketch, "E833", {"start": v(47748.82, -35390.44) * mm, "end": v(52242.4, -35381.61) * mm});
            skLineSegment(sketch, "E834", {"start": v(53004.25, -34616.45) * mm, "end": v(53004.85, -32837.3) * mm});
            skLineSegment(sketch, "E835", {"start": v(52244.25, -32076) * mm, "end": v(47927.14, -32078.15) * mm});
            skLineSegment(sketch, "E836", {"start": v(47157.12, -31316.99) * mm, "end": v(47161.28, -26745.1) * mm});
            skLineSegment(sketch, "E837", {"start": v(42078.74, -31316.26) * mm, "end": v(42082.18, -26744.8) * mm});
            skLineSegment(sketch, "E838", {"start": v(41323.31, -32079.12) * mm, "end": v(36999.88, -32083.6) * mm});
            skLineSegment(sketch, "E839", {"start": v(37002.14, -25981.13) * mm, "end": v(41321.78, -25981.26) * mm});
            skLineSegment(sketch, "E840", {"start": v(47923.48, -25981.14) * mm, "end": v(52242.61, -25982.56) * mm});
            skLineSegment(sketch, "E841", {"start": v(53004.06, -25220.93) * mm, "end": v(53009.1, -9978.39) * mm});
            skLineSegment(sketch, "E842", {"start": v(47921.53, -9214.39) * mm, "end": v(52239.4, -9216.86) * mm});
            skLineSegment(sketch, "E843", {"start": v(47160.62, -8461.36) * mm, "end": v(47163.08, -3891) * mm});
            skLineSegment(sketch, "E844", {"start": v(42081.94, -3885.17) * mm, "end": v(42079.99, -8453.85) * mm});
            skLineSegment(sketch, "E845", {"start": v(41316.15, -9212.13) * mm, "end": v(36999.9, -9217.34) * mm});
            skLineSegment(sketch, "E846", {"start": v(36239.33, -9978.11) * mm, "end": v(36240.25, -25222.08) * mm});
            skLineSegment(sketch, "E847", {"start": v(37002.98, -3123.62) * mm, "end": v(41317.73, -3124.22) * mm});
            skLineSegment(sketch, "E848", {"start": v(36239.34, -2362.8) * mm, "end": v(36239.55, -582.06) * mm});
            skLineSegment(sketch, "E849", {"start": v(37001.27, 179.29) * mm, "end": v(52239.62, 180.82) * mm});
            skLineSegment(sketch, "E850", {"start": v(53003.86, -2361.44) * mm, "end": v(53004.05, -583.24) * mm});
            skLineSegment(sketch, "E851", {"start": v(52242.01, -3123.24) * mm, "end": v(47923.59, -3121.86) * mm});
            skCircle(sketch, "E852", {"center": v(44622.12, -18998.07) * mm, "radius": 61.38 * mm});
            skCircle(sketch, "E853", {"center": v(43225.08, -17601.1) * mm, "radius": 61.38 * mm});
            skCircle(sketch, "E854", {"center": v(44622.1, -16204.2) * mm, "radius": 61.38 * mm});
            skCircle(sketch, "E855", {"center": v(46019, -17601) * mm, "radius": 61.38 * mm});
            skSolve(sketch);
        }
        {
            var Q0;
            Q0 = qSketchRegion(id + "F1", true);
            extrude(context, id + "F2", {"entities" : qUnion([Q0]), "depth" : 25 * mm});
        }
    });
